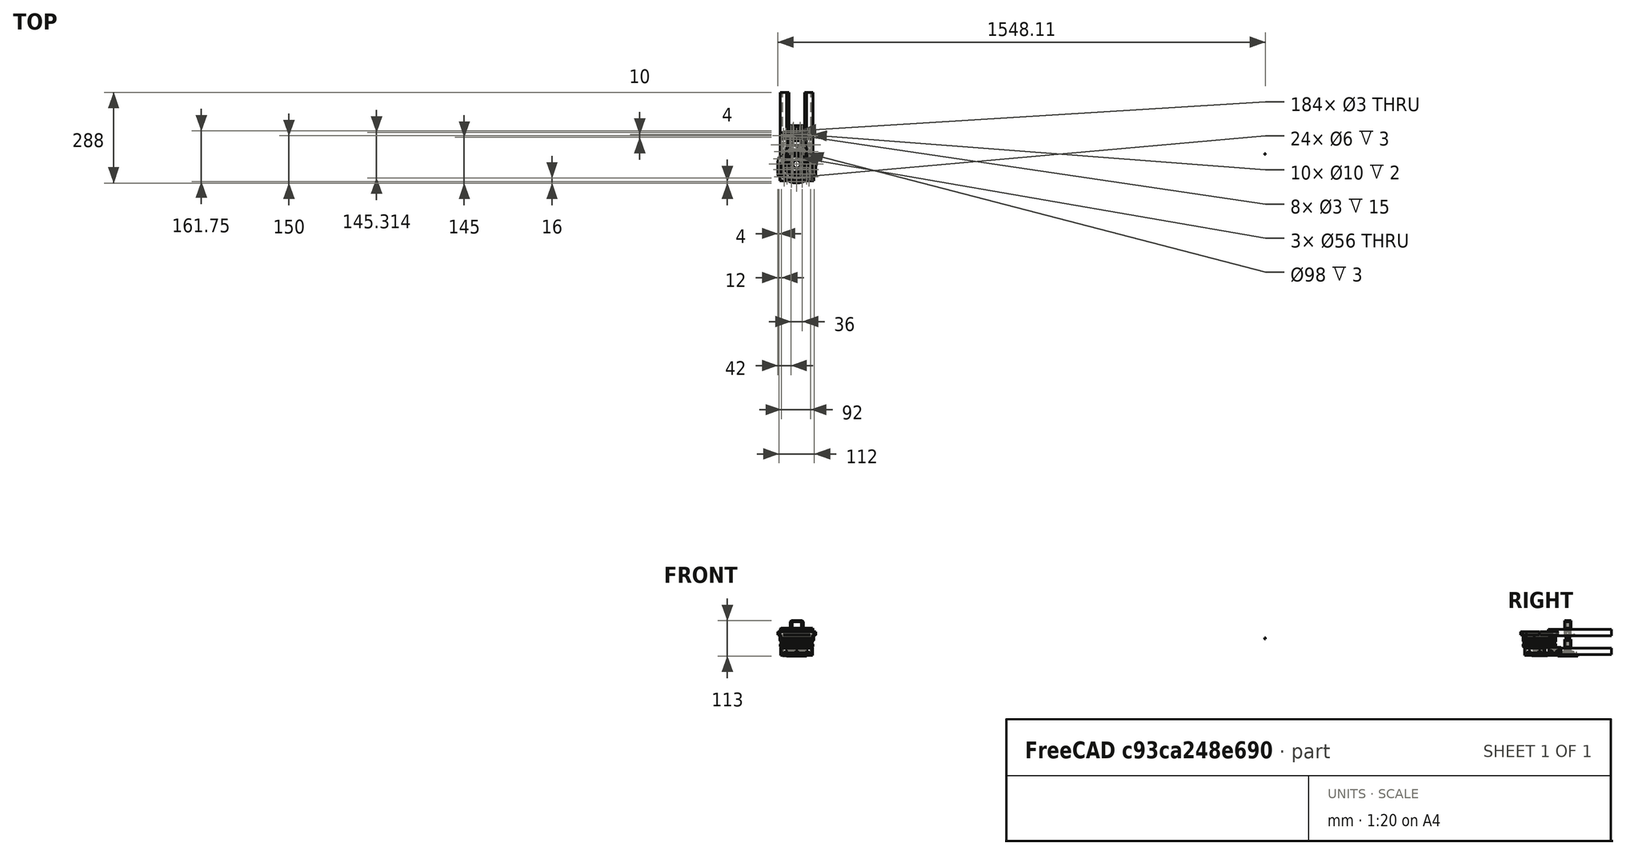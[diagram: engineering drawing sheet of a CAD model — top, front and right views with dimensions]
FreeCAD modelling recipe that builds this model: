
FCSTD DOCUMENT  (FreeCAD 0.19R24276 (Git))
Label: J-midi_encoder_002
License: All rights reserved
LicenseURL: http://en.wikipedia.org/wiki/All_rights_reserved
objects: Part::Cylinder×313, Part::Compound×126, Part::Cut×123, Part::Box×111, Part::Chamfer×32, Part::FeaturePython×23, Part::MultiFuse×6, Mesh::Feature×6, Part::Fillet×5, Part::Mirroring×2
note: 741 computed .brp shape members not serialized (recipe doc carries the construction recipe); baked Part::Feature solids carry a one-line shape summary decoded from their .brp

FEATURE [Part::Cylinder] Cylinder120  label="Válec120"
  Angle = 360
  AttacherType = Attacher::AttachEngine3D
  Height = 10
  Radius = 52
FEATURE [Part::Cylinder] Cylinder121  label="Válec121"
  Angle = 360
  AttacherType = Attacher::AttachEngine3D
  Height = 10
  Radius = 60
FEATURE [Part::FeaturePython] wormgear026  # WARN: FeaturePython — macro-defined, semantics opaque (R4)
  AttacherType = Attacher::AttachEngine3D
  beta = 29.7292
  clearance = 0.25
  diameter = 78.8
  head = 0
  height = 20
  module = 1
  pressure_angle = 20
  reverse_pitch = true
  teeth = 45
  version = 0.0.3
FEATURE [Part::Cut] Cut057
  Base = -> Cylinder121
  Placement = pos=(0,0,10) rot=(0,0,1;0.034907rad)
  Tool = -> wormgear026
FEATURE [Part::FeaturePython] wormgear027  # WARN: FeaturePython — macro-defined, semantics opaque (R4)
  AttacherType = Attacher::AttachEngine3D
  Placement = pos=(0,0,0) rot=(0,0,1;0.009355rad)
  beta = 29.7292
  clearance = 0.25
  diameter = 78.8
  head = 0
  height = 20
  module = 1
  pressure_angle = 20
  reverse_pitch = false
  teeth = 45
  version = 0.0.3
FEATURE [Part::Cut] Cut056
  Base = -> Cylinder120
  Tool = -> wormgear027
FEATURE [Part::Compound] Compound157
  Links = -> [Cut057,Cut056]
FEATURE [Part::Cylinder] Cylinder132  label="Válec132"
  Angle = 360
  AttacherType = Attacher::AttachEngine3D
  Height = 40
  Placement = pos=(59,-17,0) rot=(0,0,1;0rad)
  Radius = 10
FEATURE [Part::Cylinder] Cylinder133  label="Válec133"
  Angle = 360
  AttacherType = Attacher::AttachEngine3D
  Height = 40
  Placement = pos=(-59,-17,0) rot=(0,0,1;0rad)
  Radius = 10
FEATURE [Part::Compound] Compound162
  Links = -> [Cylinder132,Cylinder133]
FEATURE [Part::Cylinder] Cylinder134  label="Válec134"
  Angle = 360
  AttacherType = Attacher::AttachEngine3D
  Height = 10
  Placement = pos=(0,0,20) rot=(0,0,1;0rad)
  Radius = 52
FEATURE [Part::Box] Box045  label="Krychle045"
  AttacherType = Attacher::AttachEngine3D
  Height = 10
  Length = 108
  Placement = pos=(-54,-53,20) rot=(0,0,1;0rad)
  Width = 36
FEATURE [Part::Cut] Cut062
  Base = -> Box045
  Placement = pos=(0,0,-20) rot=(0,0,1;0rad)
  Tool = -> Cylinder134
FEATURE [Part::Cut] Cut063
  Base = -> Cut062
  Tool = -> Compound162
FEATURE [Part::Cylinder] Cylinder135  label="Válec135"
  Angle = 360
  AttacherType = Attacher::AttachEngine3D
  Height = 10
  Placement = pos=(0,0,20) rot=(0,0,1;0rad)
  Radius = 52
FEATURE [Part::Box] Box046  label="Krychle046"
  AttacherType = Attacher::AttachEngine3D
  Height = 10
  Length = 108
  Placement = pos=(-54,-53,20) rot=(0,0,1;0rad)
  Width = 36
FEATURE [Part::Cut] Cut064
  Base = -> Box046
  Placement = pos=(0,0,-10) rot=(0,0,1;0rad)
  Tool = -> Cylinder135
FEATURE [Part::Cylinder] Cylinder136  label="Válec136"
  Angle = 360
  AttacherType = Attacher::AttachEngine3D
  Height = 20
  Placement = pos=(-24,-40,-5) rot=(1,0,0;1.5708rad)
  Radius = 1.5
FEATURE [Part::Cylinder] Cylinder137  label="Válec137"
  Angle = 360
  AttacherType = Attacher::AttachEngine3D
  Height = 20
  Placement = pos=(24,-40,-5) rot=(1,0,0;1.5708rad)
  Radius = 1.5
FEATURE [Part::Box] Box047  label="Krychle047"
  AttacherType = Attacher::AttachEngine3D
  Height = 6
  Length = 6
  Placement = pos=(-27,-47,-8) rot=(0,0,1;0rad)
  Width = 2
FEATURE [Part::Box] Box048  label="Krychle048"
  AttacherType = Attacher::AttachEngine3D
  Height = 6
  Length = 6
  Placement = pos=(21,-47,-8) rot=(0,0,1;0rad)
  Width = 2
FEATURE [Part::FeaturePython] Tube  # WARN: FeaturePython — macro-defined, semantics opaque (R4)
  AttacherType = Attacher::AttachEngine3D
  Height = 8
  InnerRadius = 42
  OuterRadius = 52
  Placement = pos=(0,0,-8) rot=(0,0,1;0rad)
FEATURE [Part::Box] Box049  label="Krychle049"
  AttacherType = Attacher::AttachEngine3D
  Height = 6
  Length = 6
  Placement = pos=(48,-45,4) rot=(0,0,1;0rad)
  Width = 2
FEATURE [Part::Cylinder] Cylinder138  label="Válec138"
  Angle = 360
  AttacherType = Attacher::AttachEngine3D
  Height = 40
  Placement = pos=(59,-17,0) rot=(0,0,1;0rad)
  Radius = 10
FEATURE [Part::Cylinder] Cylinder139  label="Válec139"
  Angle = 360
  AttacherType = Attacher::AttachEngine3D
  Height = 40
  Placement = pos=(-59,-17,0) rot=(0,0,1;0rad)
  Radius = 10
FEATURE [Part::Cylinder] Cylinder140  label="Válec140"
  Angle = 360
  AttacherType = Attacher::AttachEngine3D
  Height = 8
  Placement = pos=(0,0,20) rot=(0,0,1;0rad)
  Radius = 52
FEATURE [Part::Compound] Compound163
  Links = -> [Cylinder138,Cylinder139]
FEATURE [Part::Box] Box050  label="Krychle050"
  AttacherType = Attacher::AttachEngine3D
  Height = 8
  Length = 108
  Placement = pos=(-54,-53,20) rot=(0,0,1;0rad)
  Width = 36
FEATURE [Part::Cut] Cut065
  Base = -> Box050
  Placement = pos=(0,0,-20) rot=(0,0,1;0rad)
  Tool = -> Cylinder140
FEATURE [Part::Cut] Cut066
  Base = -> Cut065
  Placement = pos=(0,0,-8) rot=(0,0,1;0rad)
  Tool = -> Compound163
FEATURE [Part::Cylinder] Cylinder141  label="Válec141"
  Angle = 360
  AttacherType = Attacher::AttachEngine3D
  Height = 20
  Placement = pos=(51,-40,7) rot=(1,0,0;1.5708rad)
  Radius = 1.5
FEATURE [Part::Box] Box051  label="Krychle051"
  AttacherType = Attacher::AttachEngine3D
  Height = 6
  Length = 6
  Placement = pos=(-54,-45,4) rot=(0,0,1;0rad)
  Width = 2
FEATURE [Part::Compound] Compound169
  Links = -> [Box047,Box048,Box049,Box051]
FEATURE [Part::Cylinder] Cylinder142  label="Válec142"
  Angle = 360
  AttacherType = Attacher::AttachEngine3D
  Height = 20
  Placement = pos=(-51,-40,7) rot=(1,0,0;1.5708rad)
  Radius = 1.5
FEATURE [Part::Compound] Compound172
  Links = -> [Cylinder136,Cylinder137,Cylinder141,Cylinder142]
FEATURE [Part::Cylinder] Cylinder143  label="Válec143"
  Angle = 360
  AttacherType = Attacher::AttachEngine3D
  Height = 20
  Placement = pos=(0,-56,2) rot=(0,0,1;0rad)
  Radius = 1.5
FEATURE [Part::Cylinder] Cylinder144  label="Válec144"
  Angle = 360
  AttacherType = Attacher::AttachEngine3D
  Height = 20
  Placement = pos=(39.598,-39.598,2) rot=(0,0,1;0.785398rad)
  Radius = 1.5
FEATURE [Part::Cylinder] Cylinder145  label="Válec145"
  Angle = 360
  AttacherType = Attacher::AttachEngine3D
  Height = 20
  Placement = pos=(56,0,2) rot=(0,0,1;1.5708rad)
  Radius = 1.5
FEATURE [Part::Cylinder] Cylinder146  label="Válec146"
  Angle = 360
  AttacherType = Attacher::AttachEngine3D
  Height = 20
  Placement = pos=(39.598,39.598,2) rot=(0,0,1;2.35619rad)
  Radius = 1.5
FEATURE [Part::Cylinder] Cylinder147  label="Válec147"
  Angle = 360
  AttacherType = Attacher::AttachEngine3D
  Height = 20
  Placement = pos=(-1.2e-14,56,2) rot=(0,0,1;3.14159rad)
  Radius = 1.5
FEATURE [Part::Cylinder] Cylinder148  label="Válec148"
  Angle = 360
  AttacherType = Attacher::AttachEngine3D
  Height = 20
  Placement = pos=(-39.598,39.598,2) rot=(0,0,1;3.92699rad)
  Radius = 1.5
FEATURE [Part::Cylinder] Cylinder149  label="Válec149"
  Angle = 360
  AttacherType = Attacher::AttachEngine3D
  Height = 20
  Placement = pos=(-56,-1.3e-14,2) rot=(0,0,-1;1.5708rad)
  Radius = 1.5
FEATURE [Part::Cylinder] Cylinder150  label="Válec150"
  Angle = 360
  AttacherType = Attacher::AttachEngine3D
  Height = 20
  Placement = pos=(-39.598,-39.598,2) rot=(0,0,-1;0.785398rad)
  Radius = 1.5
FEATURE [Part::Compound] Compound164
  Links = -> [Cylinder143,Cylinder144,Cylinder145,Cylinder146,Cylinder147,Cylinder148,Cylinder149,Cylinder150]
FEATURE [Part::Cut] Cut067
  Base = -> Compound157
  Tool = -> Compound164
FEATURE [Part::Cylinder] Cylinder151  label="Válec151"
  Angle = 360
  AttacherType = Attacher::AttachEngine3D
  Height = 20
  Placement = pos=(-39.598,39.598,2) rot=(0,0,1;3.92699rad)
  Radius = 1.5
FEATURE [Part::Cylinder] Cylinder152  label="Válec152"
  Angle = 360
  AttacherType = Attacher::AttachEngine3D
  Height = 20
  Placement = pos=(-39.598,-39.598,2) rot=(0,0,-1;0.785398rad)
  Radius = 1.5
FEATURE [Part::Cylinder] Cylinder153  label="Válec153"
  Angle = 360
  AttacherType = Attacher::AttachEngine3D
  Height = 20
  Placement = pos=(56,0,2) rot=(0,0,1;1.5708rad)
  Radius = 1.5
FEATURE [Part::Cylinder] Cylinder154  label="Válec154"
  Angle = 360
  AttacherType = Attacher::AttachEngine3D
  Height = 20
  Placement = pos=(-1.2e-14,56,2) rot=(0,0,1;3.14159rad)
  Radius = 1.5
FEATURE [Part::Cylinder] Cylinder155  label="Válec155"
  Angle = 360
  AttacherType = Attacher::AttachEngine3D
  Height = 20
  Placement = pos=(0,-56,2) rot=(0,0,1;0rad)
  Radius = 1.5
FEATURE [Part::Cylinder] Cylinder156  label="Válec156"
  Angle = 360
  AttacherType = Attacher::AttachEngine3D
  Height = 20
  Placement = pos=(39.598,39.598,2) rot=(0,0,1;2.35619rad)
  Radius = 1.5
FEATURE [Part::Cylinder] Cylinder157  label="Válec157"
  Angle = 360
  AttacherType = Attacher::AttachEngine3D
  Height = 20
  Placement = pos=(-56,-1.3e-14,2) rot=(0,0,-1;1.5708rad)
  Radius = 1.5
FEATURE [Part::Cylinder] Cylinder158  label="Válec158"
  Angle = 360
  AttacherType = Attacher::AttachEngine3D
  Height = 20
  Placement = pos=(39.598,-39.598,2) rot=(0,0,1;0.785398rad)
  Radius = 1.5
FEATURE [Part::Compound] Compound165
  Links = -> [Cylinder155,Cylinder158,Cylinder153,Cylinder156,Cylinder154,Cylinder151,Cylinder157,Cylinder152]
FEATURE [Part::Cut] Cut068
  Base = -> Cut064
  Tool = -> Compound165
FEATURE [Part::Cylinder] Cylinder159  label="Válec159"
  Angle = 360
  AttacherType = Attacher::AttachEngine3D
  Height = 20
  Placement = pos=(-39.6,-39.6,-10) rot=(0,0,-1;0.785398rad)
  Radius = 4
FEATURE [Part::Cylinder] Cylinder160  label="Válec160"
  Angle = 360
  AttacherType = Attacher::AttachEngine3D
  Height = 20
  Placement = pos=(39.6,-39.6,-10) rot=(0,0,1;0.785398rad)
  Radius = 4
FEATURE [Part::Compound] Compound166
  Links = -> [Cylinder159,Cylinder160]
FEATURE [Part::Cylinder] Cylinder161  label="Válec161"
  Angle = 360
  AttacherType = Attacher::AttachEngine3D
  Height = 20
  Placement = pos=(39.6,-39.6,-10) rot=(0,0,1;0.785398rad)
  Radius = 4
FEATURE [Part::Cylinder] Cylinder162  label="Válec162"
  Angle = 360
  AttacherType = Attacher::AttachEngine3D
  Height = 20
  Placement = pos=(-39.6,-39.6,-10) rot=(0,0,-1;0.785398rad)
  Radius = 4
FEATURE [Part::Compound] Compound167
  Links = -> [Cylinder162,Cylinder161]
FEATURE [Part::Cut] Cut069
  Base = -> Cut067
  Tool = -> Compound166
FEATURE [Part::Cut] Cut070
  Base = -> Cut066
  Tool = -> Compound167
FEATURE [Part::Cut] Cut072
  Base = -> Cut070
  Tool = -> Compound169
FEATURE [Part::Cylinder] Cylinder163  label="Válec163"
  Angle = 360
  AttacherType = Attacher::AttachEngine3D
  Height = 20
  Placement = pos=(39.6,-39.6,-10) rot=(0,0,1;0.785398rad)
  Radius = 4
FEATURE [Part::Cylinder] Cylinder164  label="Válec164"
  Angle = 360
  AttacherType = Attacher::AttachEngine3D
  Height = 20
  Placement = pos=(-39.6,-39.6,-10) rot=(0,0,-1;0.785398rad)
  Radius = 4
FEATURE [Part::Compound] Compound168
  Links = -> [Cylinder164,Cylinder163]
FEATURE [Part::Cut] Cut071
  Base = -> Cut063
  Tool = -> Compound168
FEATURE [Part::Box] Box052  label="Krychle052"
  AttacherType = Attacher::AttachEngine3D
  Height = 6
  Length = 6
  Placement = pos=(48,-45,4) rot=(0,0,1;0rad)
  Width = 2
FEATURE [Part::Box] Box053  label="Krychle053"
  AttacherType = Attacher::AttachEngine3D
  Height = 6
  Length = 6
  Placement = pos=(17,-47,-8) rot=(0,0,1;0rad)
  Width = 2
FEATURE [Part::Box] Box054  label="Krychle054"
  AttacherType = Attacher::AttachEngine3D
  Height = 6
  Length = 6
  Placement = pos=(-23,-47,-8) rot=(0,0,1;0rad)
  Width = 2
FEATURE [Part::Box] Box055  label="Krychle055"
  AttacherType = Attacher::AttachEngine3D
  Height = 6
  Length = 6
  Placement = pos=(-54,-45,4) rot=(0,0,1;0rad)
  Width = 2
FEATURE [Part::Compound] Compound170
  Links = -> [Box054,Box053,Box052,Box055]
FEATURE [Part::Cut] Cut073
  Base = -> Cut071
  Tool = -> Compound170
FEATURE [Part::Box] Box056  label="Krychle056"
  AttacherType = Attacher::AttachEngine3D
  Height = 6
  Length = 6
  Placement = pos=(48,-45,4) rot=(0,0,1;0rad)
  Width = 2
FEATURE [Part::Box] Box057  label="Krychle057"
  AttacherType = Attacher::AttachEngine3D
  Height = 6
  Length = 6
  Placement = pos=(21,-47,-8) rot=(0,0,1;0rad)
  Width = 2
FEATURE [Part::Box] Box058  label="Krychle058"
  AttacherType = Attacher::AttachEngine3D
  Height = 6
  Length = 6
  Placement = pos=(-27,-47,-8) rot=(0,0,1;0rad)
  Width = 2
FEATURE [Part::Box] Box059  label="Krychle059"
  AttacherType = Attacher::AttachEngine3D
  Height = 6
  Length = 6
  Placement = pos=(-54,-45,4) rot=(0,0,1;0rad)
  Width = 2
FEATURE [Part::Compound] Compound171
  Links = -> [Box058,Box057,Box056,Box059]
FEATURE [Part::Cylinder] Cylinder165  label="Válec165"
  Angle = 360
  AttacherType = Attacher::AttachEngine3D
  Height = 20
  Placement = pos=(-24,-40,-5) rot=(1,0,0;1.5708rad)
  Radius = 1.5
FEATURE [Part::Cylinder] Cylinder166  label="Válec166"
  Angle = 360
  AttacherType = Attacher::AttachEngine3D
  Height = 20
  Placement = pos=(24,-40,-5) rot=(1,0,0;1.5708rad)
  Radius = 1.5
FEATURE [Part::Cut] Cut074
  Base = -> Tube
  Tool = -> Compound171
FEATURE [Part::Cut] Cut075
  Base = -> Cut074
  Tool = -> Compound172
FEATURE [Part::Cylinder] Cylinder167  label="Válec167"
  Angle = 360
  AttacherType = Attacher::AttachEngine3D
  Height = 20
  Placement = pos=(51,-40,7) rot=(1,0,0;1.5708rad)
  Radius = 1.5
FEATURE [Part::Cylinder] Cylinder168  label="Válec168"
  Angle = 360
  AttacherType = Attacher::AttachEngine3D
  Height = 20
  Placement = pos=(-51,-40,7) rot=(1,0,0;1.5708rad)
  Radius = 1.5
FEATURE [Part::Compound] Compound173
  Links = -> [Cylinder165,Cylinder166,Cylinder167,Cylinder168]
FEATURE [Part::Cut] Cut076
  Base = -> Cut072
  Tool = -> Compound173
FEATURE [Part::Cylinder] Cylinder169  label="Válec169"
  Angle = 360
  AttacherType = Attacher::AttachEngine3D
  Height = 20
  Placement = pos=(-20,-40,-5) rot=(1,0,0;1.5708rad)
  Radius = 1.5
FEATURE [Part::Cylinder] Cylinder170  label="Válec170"
  Angle = 360
  AttacherType = Attacher::AttachEngine3D
  Height = 20
  Placement = pos=(20,-40,-5) rot=(1,0,0;1.5708rad)
  Radius = 1.5
FEATURE [Part::Cylinder] Cylinder171  label="Válec171"
  Angle = 360
  AttacherType = Attacher::AttachEngine3D
  Height = 20
  Placement = pos=(51,-40,7) rot=(1,0,0;1.5708rad)
  Radius = 1.5
FEATURE [Part::Cylinder] Cylinder172  label="Válec172"
  Angle = 360
  AttacherType = Attacher::AttachEngine3D
  Height = 20
  Placement = pos=(-51,-40,7) rot=(1,0,0;1.5708rad)
  Radius = 1.5
FEATURE [Part::Compound] Compound174
  Links = -> [Cylinder169,Cylinder170,Cylinder171,Cylinder172]
FEATURE [Part::Cut] Cut077
  Base = -> Cut073
  Tool = -> Compound174
FEATURE [Part::Box] Box060  label="Krychle060"
  AttacherType = Attacher::AttachEngine3D
  Height = 2
  Length = 6
  Placement = pos=(-3,41,-4) rot=(0,0,1;0rad)
  Width = 8
FEATURE [Part::Cylinder] Cylinder173  label="Válec173"
  Angle = 360
  AttacherType = Attacher::AttachEngine3D
  Height = 20
  Placement = pos=(0,45,-18) rot=(0,0,1;0rad)
  Radius = 1.5
FEATURE [Part::Box] Box061  label="Krychle061"
  AttacherType = Attacher::AttachEngine3D
  Height = 2
  Length = 6
  Placement = pos=(-31.1127,26.8701,-4) rot=(0,0,1;0.785398rad)
  Width = 8
FEATURE [Part::Box] Box062  label="Krychle062"
  AttacherType = Attacher::AttachEngine3D
  Height = 2
  Length = 6
  Placement = pos=(-41,-3,-4) rot=(0,0,1;1.5708rad)
  Width = 8
FEATURE [Part::Box] Box063  label="Krychle063"
  AttacherType = Attacher::AttachEngine3D
  Height = 2
  Length = 6
  Placement = pos=(-26.8701,-31.1127,-4) rot=(0,0,1;2.35619rad)
  Width = 8
FEATURE [Part::Box] Box064  label="Krychle064"
  AttacherType = Attacher::AttachEngine3D
  Height = 2
  Length = 6
  Placement = pos=(3,-41,-4) rot=(0,0,1;3.14159rad)
  Width = 8
FEATURE [Part::Box] Box065  label="Krychle065"
  AttacherType = Attacher::AttachEngine3D
  Height = 2
  Length = 6
  Placement = pos=(31.1127,-26.8701,-4) rot=(0,0,1;3.92699rad)
  Width = 8
FEATURE [Part::Box] Box066  label="Krychle066"
  AttacherType = Attacher::AttachEngine3D
  Height = 2
  Length = 6
  Placement = pos=(41,3,-4) rot=(0,0,-1;1.5708rad)
  Width = 8
FEATURE [Part::Box] Box067  label="Krychle067"
  AttacherType = Attacher::AttachEngine3D
  Height = 2
  Length = 6
  Placement = pos=(26.8701,31.1127,-4) rot=(0,0,-1;0.785398rad)
  Width = 8
FEATURE [Part::Cylinder] Cylinder174  label="Válec174"
  Angle = 360
  AttacherType = Attacher::AttachEngine3D
  Height = 20
  Placement = pos=(-31.8198,31.8198,-18) rot=(0,0,1;0.785398rad)
  Radius = 1.5
FEATURE [Part::Cylinder] Cylinder175  label="Válec175"
  Angle = 360
  AttacherType = Attacher::AttachEngine3D
  Height = 20
  Placement = pos=(-45,-6e-15,-18) rot=(0,0,1;1.5708rad)
  Radius = 1.5
FEATURE [Part::Cylinder] Cylinder176  label="Válec176"
  Angle = 360
  AttacherType = Attacher::AttachEngine3D
  Height = 20
  Placement = pos=(-31.8198,-31.8198,-18) rot=(0,0,1;2.35619rad)
  Radius = 1.5
FEATURE [Part::Cylinder] Cylinder177  label="Válec177"
  Angle = 360
  AttacherType = Attacher::AttachEngine3D
  Height = 20
  Placement = pos=(1.4e-14,-45,-18) rot=(0,0,1;3.14159rad)
  Radius = 1.5
FEATURE [Part::Cylinder] Cylinder178  label="Válec178"
  Angle = 360
  AttacherType = Attacher::AttachEngine3D
  Height = 20
  Placement = pos=(31.8198,-31.8198,-18) rot=(0,0,1;3.92699rad)
  Radius = 1.5
FEATURE [Part::Compound] Compound175
  Links = -> [Box060,Box061,Box062,Box063,Box064,Box065,Box066,Box067]
  Placement = pos=(0,0,0) rot=(0,0,1;0.392699rad)
FEATURE [Part::Cut] Cut078
  Base = -> Cut075
  Tool = -> Compound175
FEATURE [Part::Cylinder] Cylinder179  label="Válec179"
  Angle = 360
  AttacherType = Attacher::AttachEngine3D
  Height = 20
  Placement = pos=(45,1.9e-14,-18) rot=(0,0,-1;1.5708rad)
  Radius = 1.5
FEATURE [Part::Cylinder] Cylinder180  label="Válec180"
  Angle = 360
  AttacherType = Attacher::AttachEngine3D
  Height = 20
  Placement = pos=(31.8198,31.8198,-18) rot=(0,0,-1;0.785398rad)
  Radius = 1.5
FEATURE [Part::Compound] Compound176
  Links = -> [Cylinder173,Cylinder174,Cylinder175,Cylinder176,Cylinder177,Cylinder178,Cylinder179,Cylinder180]
  Placement = pos=(0,0,0) rot=(0,0,1;0.392699rad)
FEATURE [Part::Cut] Cut079
  Base = -> Cut078
  Tool = -> Compound176
FEATURE [Part::Compound] Compound177  label="joint_max_monoblok1"
  Links = -> [Cut077,Cut079,Cut076,Cut069,Cut068]
FEATURE [Part::Fillet] Fillet
  Base = -> Compound177
  Edges = 2 edges r=9: [Edge42,Edge278]
FEATURE [Part::Fillet] Fillet001  label="J-max_monoblok2"
  Base = -> Fillet
  Edges = 2 edges r=8: [Edge30,Edge90]
FEATURE [Part::Box] Box108  label="Krychle108"
  AttacherType = Attacher::AttachEngine3D
  Height = 10
  Length = 10
  Placement = pos=(50,-43,10) rot=(0,0,1;0rad)
  Width = 43
FEATURE [Part::Cylinder] Cylinder300  label="Válec300"
  Angle = 360
  AttacherType = Attacher::AttachEngine3D
  Height = 10
  Placement = pos=(60,-43,10) rot=(0,0,1;0rad)
  Radius = 6
FEATURE [Part::Box] Box109  label="Krychle109"
  AttacherType = Attacher::AttachEngine3D
  Height = 10
  Length = 10
  Placement = pos=(-60,-43,10) rot=(0,0,1;0rad)
  Width = 43
FEATURE [Part::Cylinder] Cylinder301  label="Válec301"
  Angle = 360
  AttacherType = Attacher::AttachEngine3D
  Height = 10
  Placement = pos=(-60,-43,10) rot=(0,0,1;0rad)
  Radius = 6
FEATURE [Part::Cylinder] Cylinder302  label="Válec302"
  Angle = 360
  AttacherType = Attacher::AttachEngine3D
  Height = 20
  Placement = pos=(39.598,-39.598,2) rot=(0,0,1;0.785398rad)
  Radius = 1.5
FEATURE [Part::Cylinder] Cylinder303  label="Válec303"
  Angle = 360
  AttacherType = Attacher::AttachEngine3D
  Height = 20
  Placement = pos=(39.598,39.598,2) rot=(0,0,1;2.35619rad)
  Radius = 1.5
FEATURE [Part::Compound] Compound239
  Links = -> [Box109,Box108]
FEATURE [Part::Compound] Compound241
  Links = -> [Cylinder300,Cylinder301]
FEATURE [Part::Cylinder] Cylinder304  label="Válec304"
  Angle = 360
  AttacherType = Attacher::AttachEngine3D
  Height = 20
  Placement = pos=(-39.598,39.598,2) rot=(0,0,1;3.92699rad)
  Radius = 1.5
FEATURE [Part::Cylinder] Cylinder305  label="Válec305"
  Angle = 360
  AttacherType = Attacher::AttachEngine3D
  Height = 20
  Placement = pos=(-39.598,-39.598,2) rot=(0,0,-1;0.785398rad)
  Radius = 1.5
FEATURE [Part::Cylinder] Cylinder306  label="Válec306"
  Angle = 360
  AttacherType = Attacher::AttachEngine3D
  Height = 20
  Placement = pos=(56,0,2) rot=(0,0,1;1.5708rad)
  Radius = 1.5
FEATURE [Part::Cylinder] Cylinder307  label="Válec307"
  Angle = 360
  AttacherType = Attacher::AttachEngine3D
  Height = 20
  Placement = pos=(-1.2e-14,56,2) rot=(0,0,1;3.14159rad)
  Radius = 1.5
FEATURE [Part::Cylinder] Cylinder308  label="Válec308"
  Angle = 360
  AttacherType = Attacher::AttachEngine3D
  Height = 20
  Placement = pos=(-56,-1.3e-14,2) rot=(0,0,-1;1.5708rad)
  Radius = 1.5
FEATURE [Part::Cylinder] Cylinder309  label="Válec309"
  Angle = 360
  AttacherType = Attacher::AttachEngine3D
  Height = 20
  Placement = pos=(0,-56,2) rot=(0,0,1;0rad)
  Radius = 1.5
FEATURE [Part::Compound] Compound240
  Links = -> [Cylinder309,Cylinder302,Cylinder306,Cylinder303,Cylinder307,Cylinder304,Cylinder308,Cylinder305]
FEATURE [Part::Cut] Cut129
  Base = -> Compound239
  Tool = -> Compound240
FEATURE [Part::Cut] Cut130
  Base = -> Cut129
  Tool = -> Compound241
FEATURE [Part::Fillet] Fillet002
  Base = -> Cut130
  Edges = 2 edges r=4: [Edge4,Edge43]
FEATURE [Part::Compound] Compound242  label="J-max_monoblok"
  Links = -> [Fillet002,Fillet001]
FEATURE [Part::Cylinder] Cylinder623  label="Válec623"
  Angle = 360
  AttacherType = Attacher::AttachEngine3D
  Height = 20
  Placement = pos=(-31.8198,31.8198,-18) rot=(0,0,1;0.785398rad)
  Radius = 1.5
FEATURE [Part::Cylinder] Cylinder625  label="Válec625"
  Angle = 360
  AttacherType = Attacher::AttachEngine3D
  Height = 16
  Placement = pos=(2e-15,16,2) rot=(0,0,-1;1.1781rad)
  Radius = 1.5
FEATURE [Part::Cylinder] Cylinder626  label="Válec626"
  Angle = 360
  AttacherType = Attacher::AttachEngine3D
  Height = 16
  Placement = pos=(-16,7e-15,2) rot=(0,0,1;0.392699rad)
  Radius = 1.5
FEATURE [Part::Cylinder] Cylinder627  label="Válec627"
  Angle = 360
  AttacherType = Attacher::AttachEngine3D
  Height = 16
  Placement = pos=(-1.2e-14,-16,2) rot=(0,0,1;1.96349rad)
  Radius = 1.5
FEATURE [Part::Cylinder] Cylinder628  label="Válec628"
  Angle = 360
  AttacherType = Attacher::AttachEngine3D
  Height = 20
  Placement = pos=(0,45,-18) rot=(0,0,1;0rad)
  Radius = 1.5
FEATURE [Part::Cylinder] Cylinder629  label="Válec629"
  Angle = 360
  AttacherType = Attacher::AttachEngine3D
  Height = 20
  Placement = pos=(-31.8198,-31.8198,-18) rot=(0,0,1;2.35619rad)
  Radius = 1.5
FEATURE [Part::Cylinder] Cylinder630  label="Válec630"
  Angle = 360
  AttacherType = Attacher::AttachEngine3D
  Height = 16
  Placement = pos=(16,0,2) rot=(0,0,1;3.53429rad)
  Radius = 1.5
FEATURE [Part::Compound] Compound653
  Links = -> [Cylinder630,Cylinder625,Cylinder626,Cylinder627]
  Placement = pos=(0,0,-111) rot=(0,0,1;0rad)
FEATURE [Part::Cylinder] Cylinder631  label="Válec631"
  Angle = 360
  AttacherType = Attacher::AttachEngine3D
  Height = 20
  Placement = pos=(45,1.9e-14,-18) rot=(0,0,-1;1.5708rad)
  Radius = 1.5
FEATURE [Part::Cylinder] Cylinder632  label="Válec632"
  Angle = 360
  AttacherType = Attacher::AttachEngine3D
  Height = 20
  Placement = pos=(-45,-6e-15,-18) rot=(0,0,1;1.5708rad)
  Radius = 1.5
FEATURE [Part::Cylinder] Cylinder633  label="Válec633"
  Angle = 360
  AttacherType = Attacher::AttachEngine3D
  Height = 20
  Placement = pos=(31.8198,31.8198,-18) rot=(0,0,-1;0.785398rad)
  Radius = 1.5
FEATURE [Part::Cylinder] Cylinder638  label="Válec638"
  Angle = 360
  AttacherType = Attacher::AttachEngine3D
  Height = 20
  Placement = pos=(31.8198,-31.8198,-18) rot=(0,0,1;3.92699rad)
  Radius = 1.5
FEATURE [Part::Cylinder] Cylinder639  label="Válec639"
  Angle = 360
  AttacherType = Attacher::AttachEngine3D
  Height = 20
  Placement = pos=(1.4e-14,-45,-18) rot=(0,0,1;3.14159rad)
  Radius = 1.5
FEATURE [Part::Compound] Compound654
  Links = -> [Cylinder628,Cylinder623,Cylinder632,Cylinder629,Cylinder639,Cylinder638,Cylinder631,Cylinder633]
  Placement = pos=(0,0,-87) rot=(0,0,1;0.392699rad)
FEATURE [Part::FeaturePython] Tube038  # WARN: FeaturePython — macro-defined, semantics opaque (R4)
  AttacherType = Attacher::AttachEngine3D
  Height = 2
  InnerRadius = 12
  OuterRadius = 52
  Placement = pos=(0,0,-100) rot=(0,0,1;0rad)
FEATURE [Part::FeaturePython] Tube040  # WARN: FeaturePython — macro-defined, semantics opaque (R4)
  AttacherType = Attacher::AttachEngine3D
  Height = 3
  InnerRadius = 42
  OuterRadius = 52
  Placement = pos=(0,0,-11) rot=(0,0,1;0rad)
FEATURE [Part::Cut] Cut285
  Base = -> Tube038
  Tool = -> Compound653
FEATURE [Part::Cut] Cut287
  Base = -> Cut285
  Tool = -> Compound654
FEATURE [Part::Cylinder] Cylinder652  label="Válec652"
  Angle = 360
  AttacherType = Attacher::AttachEngine3D
  Height = 20
  Placement = pos=(-31.8198,-31.8198,-18) rot=(0,0,1;2.35619rad)
  Radius = 1.5
FEATURE [Part::Cylinder] Cylinder653  label="Válec653"
  Angle = 360
  AttacherType = Attacher::AttachEngine3D
  Height = 20
  Placement = pos=(0,45,-18) rot=(0,0,1;0rad)
  Radius = 1.5
FEATURE [Part::Cylinder] Cylinder654  label="Válec654"
  Angle = 360
  AttacherType = Attacher::AttachEngine3D
  Height = 20
  Placement = pos=(45,1.9e-14,-18) rot=(0,0,-1;1.5708rad)
  Radius = 1.5
FEATURE [Part::Cylinder] Cylinder655  label="Válec655"
  Angle = 360
  AttacherType = Attacher::AttachEngine3D
  Height = 20
  Placement = pos=(1.4e-14,-45,-18) rot=(0,0,1;3.14159rad)
  Radius = 1.5
FEATURE [Part::Cylinder] Cylinder656  label="Válec656"
  Angle = 360
  AttacherType = Attacher::AttachEngine3D
  Height = 20
  Placement = pos=(31.8198,31.8198,-18) rot=(0,0,-1;0.785398rad)
  Radius = 1.5
FEATURE [Part::Cylinder] Cylinder657  label="Válec657"
  Angle = 360
  AttacherType = Attacher::AttachEngine3D
  Height = 20
  Placement = pos=(31.8198,-31.8198,-18) rot=(0,0,1;3.92699rad)
  Radius = 1.5
FEATURE [Part::Cylinder] Cylinder658  label="Válec658"
  Angle = 360
  AttacherType = Attacher::AttachEngine3D
  Height = 20
  Placement = pos=(-31.8198,31.8198,-18) rot=(0,0,1;0.785398rad)
  Radius = 1.5
FEATURE [Part::Cylinder] Cylinder659  label="Válec659"
  Angle = 360
  AttacherType = Attacher::AttachEngine3D
  Height = 20
  Placement = pos=(-45,-6e-15,-18) rot=(0,0,1;1.5708rad)
  Radius = 1.5
FEATURE [Part::Compound] Compound660
  Links = -> [Cylinder653,Cylinder658,Cylinder659,Cylinder652,Cylinder655,Cylinder657,Cylinder654,Cylinder656]
  Placement = pos=(0,0,0) rot=(0,0,1;0.392699rad)
FEATURE [Part::Cut] Cut290  label="J-max_motor-high-washer_A1"
  Base = -> Tube040
  Placement = pos=(0,0,-4) rot=(0,0,1;0rad)
  Tool = -> Compound660
FEATURE [Part::Chamfer] Chamfer018  label="J-max_motor-high-washer_A"
  Base = -> Cut290
  Edges = 1 edges r=1: [Edge3]
  Placement = pos=(0,0,4) rot=(0,0,1;0rad)
FEATURE [Part::Cylinder] Cylinder660  label="Válec660"
  Angle = 360
  AttacherType = Attacher::AttachEngine3D
  Height = 20
  Placement = pos=(0,45,-18) rot=(0,0,1;0rad)
  Radius = 1.5
FEATURE [Part::Cylinder] Cylinder661  label="Válec661"
  Angle = 360
  AttacherType = Attacher::AttachEngine3D
  Height = 20
  Placement = pos=(-31.8198,-31.8198,-18) rot=(0,0,1;2.35619rad)
  Radius = 1.5
FEATURE [Part::Cylinder] Cylinder662  label="Válec662"
  Angle = 360
  AttacherType = Attacher::AttachEngine3D
  Height = 20
  Placement = pos=(-31.8198,31.8198,-18) rot=(0,0,1;0.785398rad)
  Radius = 1.5
FEATURE [Part::Cylinder] Cylinder663  label="Válec663"
  Angle = 360
  AttacherType = Attacher::AttachEngine3D
  Height = 20
  Placement = pos=(1.4e-14,-45,-18) rot=(0,0,1;3.14159rad)
  Radius = 1.5
FEATURE [Part::Cylinder] Cylinder664  label="Válec664"
  Angle = 360
  AttacherType = Attacher::AttachEngine3D
  Height = 20
  Placement = pos=(-45,-6e-15,-18) rot=(0,0,1;1.5708rad)
  Radius = 1.5
FEATURE [Part::Cylinder] Cylinder665  label="Válec665"
  Angle = 360
  AttacherType = Attacher::AttachEngine3D
  Height = 20
  Placement = pos=(45,1.9e-14,-18) rot=(0,0,-1;1.5708rad)
  Radius = 1.5
FEATURE [Part::Cylinder] Cylinder666  label="Válec666"
  Angle = 360
  AttacherType = Attacher::AttachEngine3D
  Height = 20
  Placement = pos=(31.8198,31.8198,-18) rot=(0,0,-1;0.785398rad)
  Radius = 1.5
FEATURE [Part::Cylinder] Cylinder667  label="Válec667"
  Angle = 360
  AttacherType = Attacher::AttachEngine3D
  Height = 20
  Placement = pos=(31.8198,-31.8198,-18) rot=(0,0,1;3.92699rad)
  Radius = 1.5
FEATURE [Part::Compound] Compound661
  Links = -> [Cylinder660,Cylinder662,Cylinder664,Cylinder661,Cylinder663,Cylinder667,Cylinder665,Cylinder666]
  Placement = pos=(0,0,-8) rot=(0,0,1;0.392699rad)
FEATURE [Part::FeaturePython] Tube041  # WARN: FeaturePython — macro-defined, semantics opaque (R4)
  AttacherType = Attacher::AttachEngine3D
  Height = 10
  InnerRadius = 42
  OuterRadius = 49
  Placement = pos=(0,0,-22) rot=(0,0,1;0rad)
FEATURE [Part::Cut] Cut291
  Base = -> Tube041
  Placement = pos=(0,0,-10) rot=(0,0,1;0rad)
  Tool = -> Compound661
FEATURE [Part::FeaturePython] Tube042  # WARN: FeaturePython — macro-defined, semantics opaque (R4)
  AttacherType = Attacher::AttachEngine3D
  Height = 3
  InnerRadius = 49
  OuterRadius = 52
  Placement = pos=(0,0,-22) rot=(0,0,1;0rad)
FEATURE [Part::Chamfer] Chamfer017
  Base = -> Tube042
  Edges = 1 edges r=1: [Edge1]
  Placement = pos=(0,0,-10) rot=(0,0,1;0rad)
FEATURE [Part::Compound] Compound662  label="J-max_motor-high-washer_B"
  Links = -> [Cut291,Chamfer017]
  Placement = pos=(0,0,11) rot=(0,0,1;0rad)
FEATURE [Part::FeaturePython] Tube060  # WARN: FeaturePython — macro-defined, semantics opaque (R4)
  AttacherType = Attacher::AttachEngine3D
  Height = 9
  InnerRadius = 31
  OuterRadius = 36
  Placement = pos=(0,0,-99) rot=(0,0,1;0rad)
FEATURE [Part::Chamfer] Chamfer019
  Base = -> Tube060
  Edges = 1 edges r=1: [Edge4]
FEATURE [Part::FeaturePython] Tube061  # WARN: FeaturePython — macro-defined, semantics opaque (R4)
  AttacherType = Attacher::AttachEngine3D
  Height = 1
  InnerRadius = 26
  OuterRadius = 36
  Placement = pos=(0,0,-98) rot=(0,0,1;0rad)
FEATURE [Part::Compound] Compound663  label="J-max_undermotor-undercover"
  Links = -> [Chamfer019,Tube061,Cut287]
  Placement = pos=(0,0,77) rot=(0,0,1;0rad)
FEATURE [Part::Box] Box104  label="Krychle104"
  AttacherType = Attacher::AttachEngine3D
  Height = 2
  Length = 10
  Placement = pos=(11,-3,6) rot=(0,0,1;0rad)
  Width = 6
FEATURE [Part::Box] Box105  label="Krychle105"
  AttacherType = Attacher::AttachEngine3D
  Height = 2
  Length = 10
  Placement = pos=(-11,3,6) rot=(0,0,1;3.14159rad)
  Width = 6
FEATURE [Part::Box] Box106  label="Krychle106"
  AttacherType = Attacher::AttachEngine3D
  Height = 2
  Length = 10
  Placement = pos=(3,11,6) rot=(0,0,1;1.5708rad)
  Width = 6
FEATURE [Part::Box] Box107  label="Krychle107"
  AttacherType = Attacher::AttachEngine3D
  Height = 2
  Length = 10
  Placement = pos=(-3,-11,6) rot=(0,0,-1;1.5708rad)
  Width = 6
FEATURE [Part::Cylinder] Cylinder272  label="Válec272"
  Angle = 360
  AttacherType = Attacher::AttachEngine3D
  Height = 16
  Placement = pos=(16,0,2) rot=(0,0,1;3.53429rad)
  Radius = 1.5
FEATURE [Part::Compound] Compound232
  Links = -> [Box104,Box106,Box105,Box107]
  Placement = pos=(0,0,-111) rot=(0,0,1;0rad)
FEATURE [Part::FeaturePython] Tube029  # WARN: FeaturePython — macro-defined, semantics opaque (R4)
  AttacherType = Attacher::AttachEngine3D
  Height = 5
  InnerRadius = 12
  OuterRadius = 52
  Placement = pos=(0,0,-100) rot=(0,0,1;0rad)
FEATURE [Part::FeaturePython] Tube030  # WARN: FeaturePython — macro-defined, semantics opaque (R4)
  AttacherType = Attacher::AttachEngine3D
  Height = 4
  InnerRadius = 12
  OuterRadius = 24.8
  Placement = pos=(0,0,-103) rot=(0,0,1;0rad)
FEATURE [Part::FeaturePython] Tube031  # WARN: FeaturePython — macro-defined, semantics opaque (R4)
  AttacherType = Attacher::AttachEngine3D
  Height = 11
  InnerRadius = 12
  OuterRadius = 20
  Placement = pos=(0,0,-111) rot=(0,0,1;0rad)
FEATURE [Part::Cylinder] Cylinder273  label="Válec273"
  Angle = 360
  AttacherType = Attacher::AttachEngine3D
  Height = 16
  Placement = pos=(-16,7e-15,2) rot=(0,0,1;0.392699rad)
  Radius = 1.5
FEATURE [Part::Cylinder] Cylinder274  label="Válec274"
  Angle = 360
  AttacherType = Attacher::AttachEngine3D
  Height = 16
  Placement = pos=(-1.2e-14,-16,2) rot=(0,0,1;1.96349rad)
  Radius = 1.5
FEATURE [Part::Cylinder] Cylinder275  label="Válec275"
  Angle = 360
  AttacherType = Attacher::AttachEngine3D
  Height = 16
  Placement = pos=(2e-15,16,2) rot=(0,0,-1;1.1781rad)
  Radius = 1.5
FEATURE [Part::Compound] Compound233
  Links = -> [Cylinder272,Cylinder275,Cylinder273,Cylinder274]
  Placement = pos=(0,0,-117) rot=(0,0,1;0rad)
FEATURE [Part::Cut] Cut124
  Base = -> Tube030
  Placement = pos=(0,0,-1) rot=(0,0,1;0rad)
  Tool = -> Compound233
FEATURE [Part::Cylinder] Cylinder276  label="Válec276"
  Angle = 360
  AttacherType = Attacher::AttachEngine3D
  Height = 16
  Placement = pos=(16,0,2) rot=(0,0,1;3.53429rad)
  Radius = 1.5
FEATURE [Part::Cylinder] Cylinder277  label="Válec277"
  Angle = 360
  AttacherType = Attacher::AttachEngine3D
  Height = 16
  Placement = pos=(-16,7e-15,2) rot=(0,0,1;0.392699rad)
  Radius = 1.5
FEATURE [Part::Cylinder] Cylinder278  label="Válec278"
  Angle = 360
  AttacherType = Attacher::AttachEngine3D
  Height = 16
  Placement = pos=(-1.2e-14,-16,2) rot=(0,0,1;1.96349rad)
  Radius = 1.5
FEATURE [Part::Cylinder] Cylinder279  label="Válec279"
  Angle = 360
  AttacherType = Attacher::AttachEngine3D
  Height = 16
  Placement = pos=(2e-15,16,2) rot=(0,0,-1;1.1781rad)
  Radius = 1.5
FEATURE [Part::Compound] Compound234
  Links = -> [Cylinder276,Cylinder279,Cylinder277,Cylinder278]
  Placement = pos=(0,0,-117) rot=(0,0,1;0rad)
FEATURE [Part::Cut] Cut123
  Base = -> Tube031
  Tool = -> Compound234
FEATURE [Part::Cut] Cut126
  Base = -> Cut123
  Tool = -> Compound232
FEATURE [Part::Cylinder] Cylinder280  label="Válec280"
  Angle = 360
  AttacherType = Attacher::AttachEngine3D
  Height = 16
  Placement = pos=(2e-15,16,2) rot=(0,0,-1;1.1781rad)
  Radius = 1.5
FEATURE [Part::Cylinder] Cylinder281  label="Válec281"
  Angle = 360
  AttacherType = Attacher::AttachEngine3D
  Height = 16
  Placement = pos=(16,0,2) rot=(0,0,1;3.53429rad)
  Radius = 1.5
FEATURE [Part::Cylinder] Cylinder282  label="Válec282"
  Angle = 360
  AttacherType = Attacher::AttachEngine3D
  Height = 16
  Placement = pos=(-16,7e-15,2) rot=(0,0,1;0.392699rad)
  Radius = 1.5
FEATURE [Part::Cylinder] Cylinder283  label="Válec283"
  Angle = 360
  AttacherType = Attacher::AttachEngine3D
  Height = 16
  Placement = pos=(-1.2e-14,-16,2) rot=(0,0,1;1.96349rad)
  Radius = 1.5
FEATURE [Part::Cylinder] Cylinder284  label="Válec284"
  Angle = 360
  AttacherType = Attacher::AttachEngine3D
  Height = 20
  Placement = pos=(-45,-6e-15,-18) rot=(0,0,1;1.5708rad)
  Radius = 1.5
FEATURE [Part::Cylinder] Cylinder285  label="Válec285"
  Angle = 360
  AttacherType = Attacher::AttachEngine3D
  Height = 20
  Placement = pos=(-31.8198,-31.8198,-18) rot=(0,0,1;2.35619rad)
  Radius = 1.5
FEATURE [Part::Cylinder] Cylinder286  label="Válec286"
  Angle = 360
  AttacherType = Attacher::AttachEngine3D
  Height = 20
  Placement = pos=(0,45,-18) rot=(0,0,1;0rad)
  Radius = 1.5
FEATURE [Part::Cylinder] Cylinder287  label="Válec287"
  Angle = 360
  AttacherType = Attacher::AttachEngine3D
  Height = 20
  Placement = pos=(45,1.9e-14,-18) rot=(0,0,-1;1.5708rad)
  Radius = 1.5
FEATURE [Part::Cylinder] Cylinder288  label="Válec288"
  Angle = 360
  AttacherType = Attacher::AttachEngine3D
  Height = 20
  Placement = pos=(-31.8198,31.8198,-18) rot=(0,0,1;0.785398rad)
  Radius = 1.5
FEATURE [Part::Cylinder] Cylinder289  label="Válec289"
  Angle = 360
  AttacherType = Attacher::AttachEngine3D
  Height = 20
  Placement = pos=(31.8198,-31.8198,-18) rot=(0,0,1;3.92699rad)
  Radius = 1.5
FEATURE [Part::Cylinder] Cylinder290  label="Válec290"
  Angle = 360
  AttacherType = Attacher::AttachEngine3D
  Height = 20
  Placement = pos=(31.8198,31.8198,-18) rot=(0,0,-1;0.785398rad)
  Radius = 1.5
FEATURE [Part::Cylinder] Cylinder291  label="Válec291"
  Angle = 360
  AttacherType = Attacher::AttachEngine3D
  Height = 20
  Placement = pos=(1.4e-14,-45,-18) rot=(0,0,1;3.14159rad)
  Radius = 1.5
FEATURE [Part::Cylinder] Cylinder292  label="Válec292"
  Angle = 360
  AttacherType = Attacher::AttachEngine3D
  Height = 3
  Placement = pos=(31.8198,-31.8198,-18) rot=(0,0,1;3.92699rad)
  Radius = 3
FEATURE [Part::Cylinder] Cylinder293  label="Válec293"
  Angle = 360
  AttacherType = Attacher::AttachEngine3D
  Height = 3
  Placement = pos=(-31.8198,-31.8198,-18) rot=(0,0,1;2.35619rad)
  Radius = 3
FEATURE [Part::Cylinder] Cylinder294  label="Válec294"
  Angle = 360
  AttacherType = Attacher::AttachEngine3D
  Height = 3
  Placement = pos=(0,45,-18) rot=(0,0,1;0rad)
  Radius = 3
FEATURE [Part::Cylinder] Cylinder295  label="Válec295"
  Angle = 360
  AttacherType = Attacher::AttachEngine3D
  Height = 3
  Placement = pos=(45,1.9e-14,-18) rot=(0,0,-1;1.5708rad)
  Radius = 3
FEATURE [Part::Cylinder] Cylinder296  label="Válec296"
  Angle = 360
  AttacherType = Attacher::AttachEngine3D
  Height = 3
  Placement = pos=(-45,-6e-15,-18) rot=(0,0,1;1.5708rad)
  Radius = 3
FEATURE [Part::Cylinder] Cylinder297  label="Válec297"
  Angle = 360
  AttacherType = Attacher::AttachEngine3D
  Height = 3
  Placement = pos=(-31.8198,31.8198,-18) rot=(0,0,1;0.785398rad)
  Radius = 3
FEATURE [Part::Cylinder] Cylinder298  label="Válec298"
  Angle = 360
  AttacherType = Attacher::AttachEngine3D
  Height = 3
  Placement = pos=(1.4e-14,-45,-18) rot=(0,0,1;3.14159rad)
  Radius = 3
FEATURE [Part::Cylinder] Cylinder299  label="Válec299"
  Angle = 360
  AttacherType = Attacher::AttachEngine3D
  Height = 3
  Placement = pos=(31.8198,31.8198,-18) rot=(0,0,-1;0.785398rad)
  Radius = 3
FEATURE [Part::Compound] Compound235
  Links = -> [Cylinder281,Cylinder280,Cylinder282,Cylinder283]
  Placement = pos=(0,0,-117) rot=(0,0,1;0rad)
FEATURE [Part::Cut] Cut125
  Base = -> Tube029
  Tool = -> Compound235
FEATURE [Part::Compound] Compound236
  Links = -> [Cylinder286,Cylinder288,Cylinder284,Cylinder285,Cylinder291,Cylinder289,Cylinder287,Cylinder290]
  Placement = pos=(0,0,-87) rot=(0,0,1;0.392699rad)
FEATURE [Part::Cut] Cut127
  Base = -> Cut125
  Tool = -> Compound236
FEATURE [Part::Compound] Compound237
  Links = -> [Cylinder294,Cylinder297,Cylinder296,Cylinder293,Cylinder298,Cylinder292,Cylinder295,Cylinder299]
  Placement = pos=(0,0,-82) rot=(0,0,1;0.392699rad)
FEATURE [Part::Cut] Cut128
  Base = -> Cut127
  Tool = -> Compound237
FEATURE [Part::Chamfer] Chamfer003
  Base = -> Cut128
  Edges = 1 edges r=1: [Edge3]
FEATURE [Part::Chamfer] Chamfer004
  Base = -> Cut126
  Edges = 1 edges r=1: [Edge6]
  Placement = pos=(0,0,-1) rot=(0,0,1;0rad)
FEATURE [Part::Compound] Compound238  label="J-max_undermotor-cover"
  Links = -> [Cut124,Chamfer003,Chamfer004]
  Placement = pos=(0,0,72) rot=(0,0,1;0rad)
FEATURE [Part::Cylinder] Cylinder073  label="Válec073"
  Angle = 360
  AttacherType = Attacher::AttachEngine3D
  Height = 4
  Placement = pos=(1500,0,-4) rot=(0,0,1;0rad)
  Radius = 1.5
FEATURE [Part::Compound] Compound116
  Links = -> [Cylinder073]
  Placement = pos=(2060.63,-1353.48,-2) rot=(0.55557,0.83147,0;3.14159rad)
FEATURE [Part::FeaturePython] Tube036  # WARN: FeaturePython — macro-defined, semantics opaque (R4)
  AttacherType = Attacher::AttachEngine3D
  Height = 15
  InnerRadius = 12
  OuterRadius = 20.1
  Placement = pos=(0,0,17) rot=(0,0,1;0rad)
FEATURE [Part::FeaturePython] Tube037  # WARN: FeaturePython — macro-defined, semantics opaque (R4)
  AttacherType = Attacher::AttachEngine3D
  Height = 9
  InnerRadius = 19.5
  OuterRadius = 24.8
  Placement = pos=(0,0,23) rot=(0,0,1;0rad)
FEATURE [Part::Cylinder] Cylinder600  label="Válec600"
  Angle = 360
  AttacherType = Attacher::AttachEngine3D
  Height = 30
  Placement = pos=(-1.2e-14,-16,2) rot=(0,0,1;1.96349rad)
  Radius = 1.5
FEATURE [Part::Cylinder] Cylinder601  label="Válec601"
  Angle = 360
  AttacherType = Attacher::AttachEngine3D
  Height = 3
  Placement = pos=(-1.2e-14,-16,2) rot=(0,0,1;1.96349rad)
  Radius = 3
FEATURE [Part::Cylinder] Cylinder602  label="Válec602"
  Angle = 360
  AttacherType = Attacher::AttachEngine3D
  Height = 3
  Placement = pos=(2e-15,16,2) rot=(0,0,-1;1.1781rad)
  Radius = 3
FEATURE [Part::Cylinder] Cylinder603  label="Válec603"
  Angle = 360
  AttacherType = Attacher::AttachEngine3D
  Height = 3
  Placement = pos=(-16,7e-15,2) rot=(0,0,1;0.392699rad)
  Radius = 3
FEATURE [Part::Cylinder] Cylinder604  label="Válec604"
  Angle = 360
  AttacherType = Attacher::AttachEngine3D
  Height = 30
  Placement = pos=(16,0,2) rot=(0,0,1;3.53429rad)
  Radius = 1.5
FEATURE [Part::Cylinder] Cylinder605  label="Válec605"
  Angle = 360
  AttacherType = Attacher::AttachEngine3D
  Height = 30
  Placement = pos=(2e-15,16,2) rot=(0,0,-1;1.1781rad)
  Radius = 1.5
FEATURE [Part::Cylinder] Cylinder606  label="Válec606"
  Angle = 360
  AttacherType = Attacher::AttachEngine3D
  Height = 30
  Placement = pos=(-16,7e-15,2) rot=(0,0,1;0.392699rad)
  Radius = 1.5
FEATURE [Part::Compound] Compound647
  Links = -> [Cylinder600,Cylinder606,Cylinder605,Cylinder604]
  Placement = pos=(0,0,-2) rot=(0,0,1;0rad)
FEATURE [Part::Cylinder] Cylinder607  label="Válec607"
  Angle = 360
  AttacherType = Attacher::AttachEngine3D
  Height = 3
  Placement = pos=(16,0,2) rot=(0,0,1;3.53429rad)
  Radius = 3
FEATURE [Part::Compound] Compound646
  Links = -> [Cylinder601,Cylinder603,Cylinder602,Cylinder607]
  Placement = pos=(0,0,27) rot=(0,0,1;0rad)
FEATURE [Part::Cut] Cut276
  Base = -> Tube036
  Tool = -> Compound646
FEATURE [Part::Cut] Cut278
  Base = -> Cut276
  Tool = -> Compound647
FEATURE [Part::Box] Box290  label="Krychle290"
  AttacherType = Attacher::AttachEngine3D
  Height = 2
  Length = 10
  Placement = pos=(-11,3,6) rot=(0,0,1;3.14159rad)
  Width = 6
FEATURE [Part::Cylinder] Cylinder608  label="Válec608"
  Angle = 360
  AttacherType = Attacher::AttachEngine3D
  Height = 30
  Placement = pos=(-1.2e-14,-16,2) rot=(0,0,1;1.96349rad)
  Radius = 1.5
FEATURE [Part::Cylinder] Cylinder609  label="Válec609"
  Angle = 360
  AttacherType = Attacher::AttachEngine3D
  Height = 30
  Placement = pos=(16,0,2) rot=(0,0,1;3.53429rad)
  Radius = 1.5
FEATURE [Part::Cylinder] Cylinder610  label="Válec610"
  Angle = 360
  AttacherType = Attacher::AttachEngine3D
  Height = 30
  Placement = pos=(-16,7e-15,2) rot=(0,0,1;0.392699rad)
  Radius = 1.5
FEATURE [Part::Cylinder] Cylinder611  label="Válec611"
  Angle = 360
  AttacherType = Attacher::AttachEngine3D
  Height = 30
  Placement = pos=(2e-15,16,2) rot=(0,0,-1;1.1781rad)
  Radius = 1.5
FEATURE [Part::Compound] Compound648
  Links = -> [Cylinder608,Cylinder610,Cylinder611,Cylinder609]
  Placement = pos=(0,0,5) rot=(0,0,1;0.785398rad)
FEATURE [Part::Box] Box291  label="Krychle291"
  AttacherType = Attacher::AttachEngine3D
  Height = 2
  Length = 10
  Placement = pos=(11,-3,6) rot=(0,0,1;0rad)
  Width = 6
FEATURE [Part::Box] Box292  label="Krychle292"
  AttacherType = Attacher::AttachEngine3D
  Height = 2
  Length = 10
  Placement = pos=(-3,-11,6) rot=(0,0,-1;1.5708rad)
  Width = 6
FEATURE [Part::Box] Box293  label="Krychle293"
  AttacherType = Attacher::AttachEngine3D
  Height = 2
  Length = 10
  Placement = pos=(3,11,6) rot=(0,0,1;1.5708rad)
  Width = 6
FEATURE [Part::Compound] Compound650
  Links = -> [Box291,Box293,Box290,Box292]
  Placement = pos=(0,0,15) rot=(0,0,1;0.785398rad)
FEATURE [Part::Cut] Cut279
  Base = -> Cut278
  Tool = -> Compound650
FEATURE [Part::Cut] Cut277
  Base = -> Cut279
  Tool = -> Compound648
FEATURE [Part::Compound] Compound649
  Links = -> [Tube037,Cut277]
FEATURE [Part::Chamfer] Chamfer016  label="J-max_arm-bearing-fix"
  Base = -> Compound649
  Edges = 1 edges r=1: [Edge8]
  Placement = pos=(0,0,-24) rot=(1,0,0;3.14159rad)
FEATURE [Part::Box] Box294  label="Krychle294"
  AttacherType = Attacher::AttachEngine3D
  Height = 18
  Length = 32
  Placement = pos=(19,30,5) rot=(0,0,1;0rad)
  Width = 38
FEATURE [Part::Box] Box295  label="Krychle295"
  AttacherType = Attacher::AttachEngine3D
  Height = 20
  Length = 20
  Placement = pos=(-45,28,8) rot=(0,0,1;0rad)
  Width = 200
FEATURE [Part::Cylinder] Cylinder668  label="Válec668"
  Angle = 360
  AttacherType = Attacher::AttachEngine3D
  Height = 20
  Placement = pos=(11,54.5,3) rot=(0,0,1;0rad)
  Radius = 8
FEATURE [Part::Box] Box296  label="Krychle296"
  AttacherType = Attacher::AttachEngine3D
  Height = 18
  Length = 35
  Placement = pos=(10,36,5) rot=(0,0,1;0rad)
  Width = 17
FEATURE [Part::Box] Box297  label="Krychle297"
  AttacherType = Attacher::AttachEngine3D
  Height = 18
  Length = 11
  Placement = pos=(37,0,5) rot=(0,0,1;0rad)
  Width = 38
FEATURE [Part::Box] Box298  label="Krychle298"
  AttacherType = Attacher::AttachEngine3D
  Height = 20
  Length = 20
  Placement = pos=(25,28,8) rot=(0,0,1;0rad)
  Width = 200
FEATURE [Part::Compound] Compound210
  Links = -> [Box298,Box295]
FEATURE [Part::Box] Box299  label="Krychle299"
  AttacherType = Attacher::AttachEngine3D
  Height = 18
  Length = 32
  Placement = pos=(19,30,5) rot=(0,0,1;0rad)
  Width = 38
FEATURE [Part::Cylinder] Cylinder669  label="Válec669"
  Angle = 360
  AttacherType = Attacher::AttachEngine3D
  Height = 20
  Placement = pos=(11,54.5,3) rot=(0,0,1;0rad)
  Radius = 8
FEATURE [Part::Box] Box300  label="Krychle300"
  AttacherType = Attacher::AttachEngine3D
  Height = 18
  Length = 35
  Placement = pos=(10,36,5) rot=(0,0,1;0rad)
  Width = 17
FEATURE [Part::Box] Box301  label="Krychle301"
  AttacherType = Attacher::AttachEngine3D
  Height = 18
  Length = 11
  Placement = pos=(37,0,5) rot=(0,0,1;0rad)
  Width = 36
FEATURE [Part::Cylinder] Cylinder670  label="Válec670"
  Angle = 360
  AttacherType = Attacher::AttachEngine3D
  Height = 150
  Placement = pos=(-57,56,18) rot=(0,1,0;1.5708rad)
  Radius = 2.5
FEATURE [Part::FeaturePython] Tube012  # WARN: FeaturePython — macro-defined, semantics opaque (R4)
  AttacherType = Attacher::AttachEngine3D
  Height = 3
  InnerRadius = 28
  OuterRadius = 48
  Placement = pos=(0,0,5) rot=(0,0,1;0rad)
FEATURE [Part::FeaturePython] Tube013  # WARN: FeaturePython — macro-defined, semantics opaque (R4)
  AttacherType = Attacher::AttachEngine3D
  Height = 15
  InnerRadius = 34
  OuterRadius = 48
  Placement = pos=(0,0,8) rot=(0,0,1;0rad)
FEATURE [Part::Cut] Cut292
  Base = -> Box296
  Tool = -> Cylinder668
FEATURE [Part::MultiFuse] Fusion
  Shapes = -> [Box294,Box297,Cut292]
FEATURE [Part::Mirroring] mirror  label="Fusion (mirrored)"
  Base = (0,0,0)
  Normal = (1,0,0)
  Source = -> Fusion
FEATURE [Part::Cut] Cut293
  Base = -> Box300
  Tool = -> Cylinder669
FEATURE [Part::MultiFuse] Fusion001
  Shapes = -> [Box299,Box301,Cut293]
FEATURE [Part::MultiFuse] Fusion002
  Shapes = -> [Tube013,mirror,Fusion001]
FEATURE [Part::Cut] Cut294
  Base = -> Fusion002
  Tool = -> Compound210
FEATURE [Part::Cylinder] Cylinder671  label="Válec671"
  Angle = 360
  AttacherType = Attacher::AttachEngine3D
  Height = 30
  Placement = pos=(-57,38,18) rot=(0,1,0;1.5708rad)
  Radius = 2.5
FEATURE [Part::Cylinder] Cylinder672  label="Válec672"
  Angle = 360
  AttacherType = Attacher::AttachEngine3D
  Height = 30
  Placement = pos=(28,38,18) rot=(0,1,0;1.5708rad)
  Radius = 2.5
FEATURE [Part::Compound] Compound211
  Links = -> [Cylinder670,Cylinder671,Cylinder672]
FEATURE [Part::Cut] Cut295
  Base = -> Cut294
  Tool = -> Compound211
FEATURE [Part::Cylinder] Cylinder673  label="Válec673"
  Angle = 360
  AttacherType = Attacher::AttachEngine3D
  Height = 30
  Placement = pos=(0,44,10) rot=(0,0,-1;1.1781rad)
  Radius = 1.5
FEATURE [Part::Box] Box302  label="Krychle302"
  AttacherType = Attacher::AttachEngine3D
  Height = 2
  Length = 6
  Placement = pos=(-3,41,16) rot=(0,0,1;0rad)
  Width = 8
FEATURE [Part::Box] Box303  label="Krychle303"
  AttacherType = Attacher::AttachEngine3D
  Height = 2
  Length = 6
  Placement = pos=(-41,-3,16) rot=(0,0,1;1.5708rad)
  Width = 8
FEATURE [Part::Box] Box304  label="Krychle304"
  AttacherType = Attacher::AttachEngine3D
  Height = 2
  Length = 6
  Placement = pos=(3,-41,16) rot=(0,0,1;3.14159rad)
  Width = 8
FEATURE [Part::Box] Box305  label="Krychle305"
  AttacherType = Attacher::AttachEngine3D
  Height = 2
  Length = 6
  Placement = pos=(41,3,16) rot=(0,0,-1;1.5708rad)
  Width = 8
FEATURE [Part::Compound] Compound212
  Links = -> [Box302,Box303,Box304,Box305]
FEATURE [Part::Cut] Cut296
  Base = -> Cut295
  Tool = -> Compound212
FEATURE [Part::Cylinder] Cylinder674  label="Válec674"
  Angle = 360
  AttacherType = Attacher::AttachEngine3D
  Height = 30
  Placement = pos=(-44,0,10) rot=(0,0,1;0.392699rad)
  Radius = 1.5
FEATURE [Part::Cylinder] Cylinder675  label="Válec675"
  Angle = 360
  AttacherType = Attacher::AttachEngine3D
  Height = 30
  Placement = pos=(1.5e-14,-44,10) rot=(0,0,1;1.96349rad)
  Radius = 1.5
FEATURE [Part::Cylinder] Cylinder676  label="Válec676"
  Angle = 360
  AttacherType = Attacher::AttachEngine3D
  Height = 30
  Placement = pos=(44,3.4e-14,10) rot=(0,0,1;3.53429rad)
  Radius = 1.5
FEATURE [Part::Compound] Compound213
  Links = -> [Cylinder673,Cylinder674,Cylinder675,Cylinder676]
FEATURE [Part::Cut] Cut297
  Base = -> Cut296
  Tool = -> Compound213
FEATURE [Part::Box] Box  label="Krychle"
  AttacherType = Attacher::AttachEngine3D
  Height = 2
  Length = 6
  Placement = pos=(-51,58,12) rot=(0,0,1;0rad)
  Width = 6
FEATURE [Part::Cylinder] Cylinder  label="Válec"
  Angle = 360
  AttacherType = Attacher::AttachEngine3D
  Height = 30
  Placement = pos=(-48,61,0) rot=(0,0,1;0rad)
  Radius = 1.5
FEATURE [Part::Box] Box306  label="Krychle306"
  AttacherType = Attacher::AttachEngine3D
  Height = 2
  Length = 6
  Placement = pos=(-25,58,12) rot=(0,0,1;0rad)
  Width = 6
FEATURE [Part::Cylinder] Cylinder677  label="Válec677"
  Angle = 360
  AttacherType = Attacher::AttachEngine3D
  Height = 30
  Placement = pos=(-22,61,0) rot=(0,0,1;0rad)
  Radius = 1.5
FEATURE [Part::Box] Box307  label="Krychle307"
  AttacherType = Attacher::AttachEngine3D
  Height = 2
  Length = 6
  Placement = pos=(45,58,12) rot=(0,0,1;0rad)
  Width = 6
FEATURE [Part::Box] Box308  label="Krychle308"
  AttacherType = Attacher::AttachEngine3D
  Height = 2
  Length = 6
  Placement = pos=(19,58,12) rot=(0,0,1;0rad)
  Width = 6
FEATURE [Part::Box] Box309  label="Krychle309"
  AttacherType = Attacher::AttachEngine3D
  Height = 18
  Length = 3
  Placement = pos=(48,14,5) rot=(0,0,1;0rad)
  Width = 16
FEATURE [Part::Box] Box310  label="Krychle310"
  AttacherType = Attacher::AttachEngine3D
  Height = 18
  Length = 3
  Placement = pos=(-51,14,5) rot=(0,0,1;0rad)
  Width = 16
FEATURE [Part::Cylinder] Cylinder678  label="Válec678"
  Angle = 360
  AttacherType = Attacher::AttachEngine3D
  Height = 30
  Placement = pos=(48,61,0) rot=(0,0,1;0rad)
  Radius = 1.5
FEATURE [Part::Cylinder] Cylinder679  label="Válec679"
  Angle = 360
  AttacherType = Attacher::AttachEngine3D
  Height = 30
  Placement = pos=(22,61,0) rot=(0,0,1;0rad)
  Radius = 1.5
FEATURE [Part::Compound] Compound
  Links = -> [Cylinder,Cylinder677,Cylinder678,Cylinder679]
  Placement = pos=(0,0,7) rot=(0,0,1;0rad)
FEATURE [Part::Compound] Compound664
  Links = -> [Box,Box306,Box307,Box308]
FEATURE [Part::Cut] Cut
  Base = -> Cut297
  Tool = -> Compound664
FEATURE [Part::Cut] Cut298
  Base = -> Cut
  Tool = -> Compound
FEATURE [Part::Chamfer] Chamfer
  Base = -> Box310
  Edges = 1 edges r=2.9: [Edge1]
FEATURE [Part::Chamfer] Chamfer033
  Base = -> Box309
  Edges = 1 edges r=2.9: [Edge5]
FEATURE [Part::Cylinder] Cylinder680  label="Válec680"
  Angle = 360
  AttacherType = Attacher::AttachEngine3D
  Height = 10
  Placement = pos=(-19,56,18) rot=(0,1,0;1.5708rad)
  Radius = 8
FEATURE [Part::Cylinder] Cylinder681  label="Válec681"
  Angle = 360
  AttacherType = Attacher::AttachEngine3D
  Height = 10
  Placement = pos=(9,56,18) rot=(0,1,0;1.5708rad)
  Radius = 8
FEATURE [Part::Compound] Compound665
  Links = -> [Cylinder680,Cylinder681]
FEATURE [Part::Box] Box311  label="Krychle311"
  AttacherType = Attacher::AttachEngine3D
  Height = 2
  Length = 6
  Placement = pos=(-26.8701,-31.1127,16) rot=(0,0,1;2.35619rad)
  Width = 8
FEATURE [Part::Cylinder] Cylinder682  label="Válec682"
  Angle = 360
  AttacherType = Attacher::AttachEngine3D
  Height = 30
  Placement = pos=(-31.1127,-31.1127,10) rot=(0,0,1;1.1781rad)
  Radius = 1.5
FEATURE [Part::Box] Box312  label="Krychle312"
  AttacherType = Attacher::AttachEngine3D
  Height = 2
  Length = 6
  Placement = pos=(31.1127,-26.8701,16) rot=(0,0,1;3.92699rad)
  Width = 8
FEATURE [Part::Compound] Compound652
  Links = -> [Box311,Box312]
FEATURE [Part::Cylinder] Cylinder683  label="Válec683"
  Angle = 360
  AttacherType = Attacher::AttachEngine3D
  Height = 30
  Placement = pos=(31.1127,-31.1127,10) rot=(0,0,1;2.74889rad)
  Radius = 1.5
FEATURE [Part::Compound] Compound667
  Links = -> [Cylinder682,Cylinder683]
FEATURE [Part::Cut] Cut299
  Base = -> Cut298
  Tool = -> Compound665
FEATURE [Part::Chamfer] Chamfer034
  Base = -> Cut299
  Edges = 2 edges r=2: [Edge163,Edge202]
FEATURE [Part::Fillet] Fillet003
  Base = -> Chamfer034
  Edges = 2 edges r=3: [Edge4,Edge291]
FEATURE [Part::Compound] Compound666
  Links = -> [Chamfer,Chamfer033,Fillet003]
FEATURE [Part::Compound] Compound651
  Links = -> [Tube012,Compound666]
FEATURE [Part::Cut] Cut300
  Base = -> Compound651
  Tool = -> Compound652
FEATURE [Part::Cut] Cut301  label="J-max_bear-rotator1"
  Base = -> Cut300
  Tool = -> Compound667
FEATURE [Part::FeaturePython] Tube062  # WARN: FeaturePython — macro-defined, semantics opaque (R4)
  AttacherType = Attacher::AttachEngine3D
  Height = 3
  InnerRadius = 28
  OuterRadius = 48
  Placement = pos=(0,0,5) rot=(0,0,1;0rad)
FEATURE [Part::Compound] Compound668  label="J-max_bear-rotator"
  Links = -> [Tube062,Cut301]
  Placement = pos=(0,0,-24) rot=(0,1,0;3.14159rad)
FEATURE [Part::FeaturePython] Tube035  # WARN: FeaturePython — macro-defined, semantics opaque (R4)
  AttacherType = Attacher::AttachEngine3D
  Height = 8
  InnerRadius = 28
  OuterRadius = 34
  Placement = pos=(0,0,23) rot=(0,0,1;0rad)
FEATURE [Part::Box] Box313  label="Krychle313"
  AttacherType = Attacher::AttachEngine3D
  Height = 20
  Length = 20
  Placement = pos=(-45,28,8) rot=(0,0,1;0rad)
  Width = 200
FEATURE [Part::FeaturePython] Tube063  # WARN: FeaturePython — macro-defined, semantics opaque (R4)
  AttacherType = Attacher::AttachEngine3D
  Height = 8
  InnerRadius = 34
  OuterRadius = 48
  Placement = pos=(0,0,23) rot=(0,0,1;0rad)
FEATURE [Part::Box] Box314  label="Krychle314"
  AttacherType = Attacher::AttachEngine3D
  Height = 8
  Length = 32
  Placement = pos=(19,30,5) rot=(0,0,1;0rad)
  Width = 38
FEATURE [Part::Cylinder] Cylinder612  label="Válec612"
  Angle = 360
  AttacherType = Attacher::AttachEngine3D
  Height = 20
  Placement = pos=(11,54.5,3) rot=(0,0,1;0rad)
  Radius = 8
FEATURE [Part::Box] Box315  label="Krychle315"
  AttacherType = Attacher::AttachEngine3D
  Height = 8
  Length = 35
  Placement = pos=(10,36,5) rot=(0,0,1;0rad)
  Width = 17
FEATURE [Part::Cut] Cut280
  Base = -> Box315
  Tool = -> Cylinder612
FEATURE [Part::Box] Box316  label="Krychle316"
  AttacherType = Attacher::AttachEngine3D
  Height = 8
  Length = 11
  Placement = pos=(37,0,5) rot=(0,0,1;0rad)
  Width = 38
FEATURE [Part::MultiFuse] Fusion015
  Placement = pos=(0,0,18) rot=(0,0,1;0rad)
  Shapes = -> [Box314,Box316,Cut280]
FEATURE [Part::Mirroring] mirror005  label="Fusion (mirrored)005"
  Base = (0,0,0)
  Normal = (1,0,0)
  Source = -> Fusion015
FEATURE [Part::Box] Box317  label="Krychle317"
  AttacherType = Attacher::AttachEngine3D
  Height = 20
  Length = 20
  Placement = pos=(25,28,8) rot=(0,0,1;0rad)
  Width = 200
FEATURE [Part::Compound] Compound655
  Links = -> [Box317,Box313]
FEATURE [Part::Box] Box318  label="Krychle318"
  AttacherType = Attacher::AttachEngine3D
  Height = 8
  Length = 32
  Placement = pos=(19,30,5) rot=(0,0,1;0rad)
  Width = 38
FEATURE [Part::Cylinder] Cylinder613  label="Válec613"
  Angle = 360
  AttacherType = Attacher::AttachEngine3D
  Height = 20
  Placement = pos=(11,54.5,3) rot=(0,0,1;0rad)
  Radius = 8
FEATURE [Part::Box] Box319  label="Krychle319"
  AttacherType = Attacher::AttachEngine3D
  Height = 8
  Length = 35
  Placement = pos=(10,36,5) rot=(0,0,1;0rad)
  Width = 17
FEATURE [Part::Cut] Cut281
  Base = -> Box319
  Tool = -> Cylinder613
FEATURE [Part::Box] Box320  label="Krychle320"
  AttacherType = Attacher::AttachEngine3D
  Height = 8
  Length = 11
  Placement = pos=(37,0,5) rot=(0,0,1;0rad)
  Width = 36
FEATURE [Part::MultiFuse] Fusion016
  Placement = pos=(0,0,18) rot=(0,0,1;0rad)
  Shapes = -> [Box318,Box320,Cut281]
FEATURE [Part::MultiFuse] Fusion017
  Shapes = -> [Tube063,mirror005,Fusion016]
FEATURE [Part::Cut] Cut282
  Base = -> Fusion017
  Tool = -> Compound655
FEATURE [Part::Cylinder] Cylinder614  label="Válec614"
  Angle = 360
  AttacherType = Attacher::AttachEngine3D
  Height = 150
  Placement = pos=(-57,56,18) rot=(0,1,0;1.5708rad)
  Radius = 2.5
FEATURE [Part::Cylinder] Cylinder615  label="Válec615"
  Angle = 360
  AttacherType = Attacher::AttachEngine3D
  Height = 30
  Placement = pos=(-57,38,18) rot=(0,1,0;1.5708rad)
  Radius = 2.5
FEATURE [Part::Cylinder] Cylinder616  label="Válec616"
  Angle = 360
  AttacherType = Attacher::AttachEngine3D
  Height = 30
  Placement = pos=(28,38,18) rot=(0,1,0;1.5708rad)
  Radius = 2.5
FEATURE [Part::Compound] Compound656
  Links = -> [Cylinder614,Cylinder615,Cylinder616]
FEATURE [Part::Cut] Cut283
  Base = -> Cut282
  Tool = -> Compound656
FEATURE [Part::Cylinder] Cylinder617  label="Válec617"
  Angle = 360
  AttacherType = Attacher::AttachEngine3D
  Height = 30
  Placement = pos=(0,44,10) rot=(0,0,-1;1.1781rad)
  Radius = 1.5
FEATURE [Part::Box] Box321  label="Krychle321"
  AttacherType = Attacher::AttachEngine3D
  Height = 2
  Length = 6
  Placement = pos=(-3,41,16) rot=(0,0,1;0rad)
  Width = 8
FEATURE [Part::Box] Box322  label="Krychle322"
  AttacherType = Attacher::AttachEngine3D
  Height = 2
  Length = 6
  Placement = pos=(-41,-3,16) rot=(0,0,1;1.5708rad)
  Width = 8
FEATURE [Part::Box] Box323  label="Krychle323"
  AttacherType = Attacher::AttachEngine3D
  Height = 2
  Length = 6
  Placement = pos=(3,-41,16) rot=(0,0,1;3.14159rad)
  Width = 8
FEATURE [Part::Box] Box324  label="Krychle324"
  AttacherType = Attacher::AttachEngine3D
  Height = 2
  Length = 6
  Placement = pos=(41,3,16) rot=(0,0,-1;1.5708rad)
  Width = 8
FEATURE [Part::Compound] Compound657
  Links = -> [Box321,Box322,Box323,Box324]
FEATURE [Part::Cut] Cut284
  Base = -> Cut283
  Tool = -> Compound657
FEATURE [Part::Cylinder] Cylinder618  label="Válec618"
  Angle = 360
  AttacherType = Attacher::AttachEngine3D
  Height = 30
  Placement = pos=(-44,0,10) rot=(0,0,1;0.392699rad)
  Radius = 1.5
FEATURE [Part::Cylinder] Cylinder619  label="Válec619"
  Angle = 360
  AttacherType = Attacher::AttachEngine3D
  Height = 30
  Placement = pos=(1.5e-14,-44,10) rot=(0,0,1;1.96349rad)
  Radius = 1.5
FEATURE [Part::Cylinder] Cylinder620  label="Válec620"
  Angle = 360
  AttacherType = Attacher::AttachEngine3D
  Height = 30
  Placement = pos=(44,3.4e-14,10) rot=(0,0,1;3.53429rad)
  Radius = 1.5
FEATURE [Part::Compound] Compound658
  Links = -> [Cylinder617,Cylinder618,Cylinder619,Cylinder620]
FEATURE [Part::Cut] Cut302
  Base = -> Cut284
  Tool = -> Compound658
FEATURE [Part::Box] Box325  label="Krychle325"
  AttacherType = Attacher::AttachEngine3D
  Height = 2
  Length = 6
  Placement = pos=(-51,58,12) rot=(0,0,1;0rad)
  Width = 6
FEATURE [Part::Cylinder] Cylinder621  label="Válec621"
  Angle = 360
  AttacherType = Attacher::AttachEngine3D
  Height = 30
  Placement = pos=(-48,61,0) rot=(0,0,1;0rad)
  Radius = 1.5
FEATURE [Part::Box] Box326  label="Krychle326"
  AttacherType = Attacher::AttachEngine3D
  Height = 2
  Length = 6
  Placement = pos=(-25,58,12) rot=(0,0,1;0rad)
  Width = 6
FEATURE [Part::Cylinder] Cylinder622  label="Válec622"
  Angle = 360
  AttacherType = Attacher::AttachEngine3D
  Height = 30
  Placement = pos=(-22,61,0) rot=(0,0,1;0rad)
  Radius = 1.5
FEATURE [Part::Box] Box327  label="Krychle327"
  AttacherType = Attacher::AttachEngine3D
  Height = 2
  Length = 6
  Placement = pos=(45,58,12) rot=(0,0,1;0rad)
  Width = 6
FEATURE [Part::Box] Box328  label="Krychle328"
  AttacherType = Attacher::AttachEngine3D
  Height = 2
  Length = 6
  Placement = pos=(19,58,12) rot=(0,0,1;0rad)
  Width = 6
FEATURE [Part::Compound] Compound669
  Links = -> [Box325,Box326,Box327,Box328]
FEATURE [Part::Cut] Cut286
  Base = -> Cut302
  Tool = -> Compound669
FEATURE [Part::Cylinder] Cylinder684  label="Válec684"
  Angle = 360
  AttacherType = Attacher::AttachEngine3D
  Height = 30
  Placement = pos=(48,61,0) rot=(0,0,1;0rad)
  Radius = 1.5
FEATURE [Part::Cylinder] Cylinder624  label="Válec624"
  Angle = 360
  AttacherType = Attacher::AttachEngine3D
  Height = 30
  Placement = pos=(22,61,0) rot=(0,0,1;0rad)
  Radius = 1.5
FEATURE [Part::Compound] Compound659
  Links = -> [Cylinder621,Cylinder622,Cylinder684,Cylinder624]
  Placement = pos=(0,0,7) rot=(0,0,1;0rad)
FEATURE [Part::Cut] Cut303
  Base = -> Cut286
  Tool = -> Compound659
FEATURE [Part::Cylinder] Cylinder685  label="Válec685"
  Angle = 360
  AttacherType = Attacher::AttachEngine3D
  Height = 10
  Placement = pos=(-19,56,18) rot=(0,1,0;1.5708rad)
  Radius = 8
FEATURE [Part::Cylinder] Cylinder686  label="Válec686"
  Angle = 360
  AttacherType = Attacher::AttachEngine3D
  Height = 10
  Placement = pos=(9,56,18) rot=(0,1,0;1.5708rad)
  Radius = 8
FEATURE [Part::Compound] Compound670
  Links = -> [Cylinder685,Cylinder686]
FEATURE [Part::Cut] Cut288
  Base = -> Cut303
  Tool = -> Compound670
FEATURE [Part::Cylinder] Cylinder687  label="Válec687"
  Angle = 360
  AttacherType = Attacher::AttachEngine3D
  Height = 3
  Placement = pos=(0,44,10) rot=(0,0,-1;1.1781rad)
  Radius = 3
FEATURE [Part::Cylinder] Cylinder634  label="Válec634"
  Angle = 360
  AttacherType = Attacher::AttachEngine3D
  Height = 3
  Placement = pos=(-44,0,10) rot=(0,0,1;0.392699rad)
  Radius = 3
FEATURE [Part::Cylinder] Cylinder635  label="Válec635"
  Angle = 360
  AttacherType = Attacher::AttachEngine3D
  Height = 3
  Placement = pos=(1.5e-14,-44,10) rot=(0,0,1;1.96349rad)
  Radius = 3
FEATURE [Part::Cylinder] Cylinder636  label="Válec636"
  Angle = 360
  AttacherType = Attacher::AttachEngine3D
  Height = 3
  Placement = pos=(44,3.4e-14,10) rot=(0,0,1;3.53429rad)
  Radius = 3
FEATURE [Part::Compound] Compound671
  Links = -> [Cylinder687,Cylinder634,Cylinder635,Cylinder636]
  Placement = pos=(0,0,18) rot=(0,0,1;0rad)
FEATURE [Part::Box] Box329  label="Krychle329"
  AttacherType = Attacher::AttachEngine3D
  Height = 8
  Length = 3
  Placement = pos=(-51,14,23) rot=(0,0,1;0rad)
  Width = 16
FEATURE [Part::Box] Box330  label="Krychle330"
  AttacherType = Attacher::AttachEngine3D
  Height = 8
  Length = 3
  Placement = pos=(48,14,23) rot=(0,0,1;0rad)
  Width = 16
FEATURE [Part::Cylinder] Cylinder637  label="Válec637"
  Angle = 360
  AttacherType = Attacher::AttachEngine3D
  Height = 3
  Placement = pos=(-48,61,0) rot=(0,0,1;0rad)
  Radius = 3
FEATURE [Part::Cylinder] Cylinder688  label="Válec688"
  Angle = 360
  AttacherType = Attacher::AttachEngine3D
  Height = 3
  Placement = pos=(-22,61,0) rot=(0,0,1;0rad)
  Radius = 3
FEATURE [Part::Cylinder] Cylinder689  label="Válec689"
  Angle = 360
  AttacherType = Attacher::AttachEngine3D
  Height = 3
  Placement = pos=(48,61,0) rot=(0,0,1;0rad)
  Radius = 3
FEATURE [Part::Cylinder] Cylinder640  label="Válec640"
  Angle = 360
  AttacherType = Attacher::AttachEngine3D
  Height = 3
  Placement = pos=(22,61,0) rot=(0,0,1;0rad)
  Radius = 3
FEATURE [Part::Cylinder] Cylinder641  label="Válec641"
  Angle = 360
  AttacherType = Attacher::AttachEngine3D
  Height = 30
  Placement = pos=(-31.1127,-31.1127,10) rot=(0,0,1;1.1781rad)
  Radius = 1.5
FEATURE [Part::Cylinder] Cylinder642  label="Válec642"
  Angle = 360
  AttacherType = Attacher::AttachEngine3D
  Height = 30
  Placement = pos=(31.1127,-31.1127,10) rot=(0,0,1;2.74889rad)
  Radius = 1.5
FEATURE [Part::Cylinder] Cylinder643  label="Válec643"
  Angle = 360
  AttacherType = Attacher::AttachEngine3D
  Height = 3
  Placement = pos=(-31.1127,-31.1127,10) rot=(0,0,1;1.1781rad)
  Radius = 3
FEATURE [Part::Cylinder] Cylinder644  label="Válec644"
  Angle = 360
  AttacherType = Attacher::AttachEngine3D
  Height = 3
  Placement = pos=(31.1127,-31.1127,10) rot=(0,0,1;2.74889rad)
  Radius = 3
FEATURE [Part::Compound] Compound672
  Links = -> [Cylinder637,Cylinder688,Cylinder689,Cylinder640]
  Placement = pos=(0,0,28) rot=(0,0,1;0rad)
FEATURE [Part::Compound] Compound673
  Links = -> [Cylinder641,Cylinder642]
FEATURE [Part::Compound] Compound674
  Links = -> [Cylinder643,Cylinder644]
  Placement = pos=(0,0,18) rot=(0,0,1;0rad)
FEATURE [Part::Chamfer] Chamfer035
  Base = -> Box329
  Edges = 1 edges r=2.9: [Edge1]
FEATURE [Part::Chamfer] Chamfer037
  Base = -> Box330
  Edges = 1 edges r=2.9: [Edge5]
FEATURE [Part::Cut] Cut289
  Base = -> Cut288
  Tool = -> Compound671
FEATURE [Part::Cut] Cut304
  Base = -> Cut289
  Tool = -> Compound674
FEATURE [Part::Cut] Cut305
  Base = -> Cut304
  Tool = -> Compound672
FEATURE [Part::Cut] Cut306
  Base = -> Cut305
  Tool = -> Compound673
FEATURE [Part::Chamfer] Chamfer036
  Base = -> Cut306
  Edges = 2 edges r=2: [Edge104,Edge164]
FEATURE [Part::Fillet] Fillet008
  Base = -> Chamfer036
  Edges = 2 edges r=3: [Edge6,Edge219]
FEATURE [Part::Compound] Compound675  label="J-max_bear-cover"
  Links = -> [Tube035,Chamfer035,Chamfer037,Fillet008]
  Placement = pos=(0,0,-24) rot=(0,1,0;3.14159rad)
FEATURE [Part::Box] Box331  label="Krychle331"
  AttacherType = Attacher::AttachEngine3D
  Height = 20
  Length = 20
  Placement = pos=(-45,28,8) rot=(0,0,1;0rad)
  Width = 200
FEATURE [Part::Box] Box332  label="Krychle332"
  AttacherType = Attacher::AttachEngine3D
  Height = 20
  Length = 20
  Placement = pos=(25,28,8) rot=(0,0,1;0rad)
  Width = 200
FEATURE [Part::Compound] Compound676
  Links = -> [Box332,Box331]
  Placement = pos=(0,0,-60) rot=(0,0,1;0rad)
FEATURE [Part::Box] Box333  label="Krychle333"
  AttacherType = Attacher::AttachEngine3D
  Height = 4
  Length = 90
  Placement = pos=(-45,80,-56) rot=(0,0,1;0rad)
  Width = 16
FEATURE [Part::Cylinder] Cylinder774  label="Válec774"
  Angle = 360
  AttacherType = Attacher::AttachEngine3D
  Height = 20
  Placement = pos=(15.75,114,38.52) rot=(0,0.707107,0.707107;3.14159rad)
  Radius = 1.5
FEATURE [Part::Cylinder] Cylinder776  label="Válec776"
  Angle = 360
  AttacherType = Attacher::AttachEngine3D
  Height = 20
  Placement = pos=(15.75,114,59.48) rot=(0,0.707107,0.707107;3.14159rad)
  Radius = 1.5
FEATURE [Part::Compound] Compound536
  Links = -> [Cylinder774,Cylinder776]
  Placement = pos=(-49,0,-96) rot=(0.57735,0.57735,0.57735;2.0944rad)
FEATURE [Part::Box] Box636  label="Krychle636"
  AttacherType = Attacher::AttachEngine3D
  Height = 3
  Length = 16
  Placement = pos=(-33.45,-27.55,31) rot=(0,0,1;0rad)
  Width = 8
FEATURE [Part::Cylinder] Cylinder1598  label="Válec1598"
  Angle = 360
  AttacherType = Attacher::AttachEngine3D
  Height = 4
  Placement = pos=(23.55,23.55,26) rot=(0,0,1;0rad)
  Radius = 5
FEATURE [Part::Cylinder] Cylinder1599  label="Válec1599"
  Angle = 360
  AttacherType = Attacher::AttachEngine3D
  Height = 30
  Placement = pos=(-1.2e-14,-16,2) rot=(0,0,1;1.96349rad)
  Radius = 1.5
FEATURE [Part::Cylinder] Cylinder1600  label="Válec1600"
  Angle = 360
  AttacherType = Attacher::AttachEngine3D
  Height = 20
  Placement = pos=(0,0,15) rot=(0,0,1;0rad)
  Radius = 12
FEATURE [Part::Cylinder] Cylinder1601  label="Válec1601"
  Angle = 360
  AttacherType = Attacher::AttachEngine3D
  Height = 3
  Placement = pos=(2e-15,16,2) rot=(0,0,-1;1.1781rad)
  Radius = 3
FEATURE [Part::Box] Box637  label="Krychle637"
  AttacherType = Attacher::AttachEngine3D
  Height = 3
  Length = 16
  Placement = pos=(17.55,19.55,31) rot=(0,0,1;0rad)
  Width = 8
FEATURE [Part::Cylinder] Cylinder1602  label="Válec1602"
  Angle = 360
  AttacherType = Attacher::AttachEngine3D
  Height = 20
  Placement = pos=(23.55,23.55,20) rot=(0,0,1;0rad)
  Radius = 2.5
FEATURE [Part::Cylinder] Cylinder1603  label="Válec1603"
  Angle = 360
  AttacherType = Attacher::AttachEngine3D
  Height = 30
  Placement = pos=(-16,7e-15,2) rot=(0,0,1;0.392699rad)
  Radius = 1.5
FEATURE [Part::Cylinder] Cylinder1604  label="Válec1604"
  Angle = 360
  AttacherType = Attacher::AttachEngine3D
  Height = 20
  Placement = pos=(-23.55,23.55,20) rot=(0,0,1;0rad)
  Radius = 2.5
FEATURE [Part::Cylinder] Cylinder1605  label="Válec1605"
  Angle = 360
  AttacherType = Attacher::AttachEngine3D
  Height = 4
  Placement = pos=(23.55,-23.55,26) rot=(0,0,1;0rad)
  Radius = 5
FEATURE [Part::Box] Box638  label="Krychle638"
  AttacherType = Attacher::AttachEngine3D
  Height = 8
  Length = 64
  Placement = pos=(-32,-32,26) rot=(0,0,1;0rad)
  Width = 64
FEATURE [Part::Cylinder] Cylinder1606  label="Válec1606"
  Angle = 360
  AttacherType = Attacher::AttachEngine3D
  Height = 3
  Placement = pos=(16,0,2) rot=(0,0,1;3.53429rad)
  Radius = 3
FEATURE [Part::Box] Box639  label="Krychle639"
  AttacherType = Attacher::AttachEngine3D
  Height = 3
  Length = 16
  Placement = pos=(-33.45,19.55,31) rot=(0,0,1;0rad)
  Width = 8
FEATURE [Part::Cylinder] Cylinder1607  label="Válec1607"
  Angle = 360
  AttacherType = Attacher::AttachEngine3D
  Height = 20
  Placement = pos=(23.55,-23.55,20) rot=(0,0,1;0rad)
  Radius = 2.5
FEATURE [Part::Cylinder] Cylinder1608  label="Válec1608"
  Angle = 360
  AttacherType = Attacher::AttachEngine3D
  Height = 20
  Placement = pos=(-23.55,-23.55,20) rot=(0,0,1;0rad)
  Radius = 2.5
FEATURE [Part::Compound] Compound798
  Links = -> [Cylinder1602,Cylinder1604,Cylinder1608,Cylinder1607]
FEATURE [Part::Box] Box640  label="Krychle640"
  AttacherType = Attacher::AttachEngine3D
  Height = 3
  Length = 16
  Placement = pos=(17.55,-27.55,31) rot=(0,0,1;0rad)
  Width = 8
FEATURE [Part::Cylinder] Cylinder1609  label="Válec1609"
  Angle = 360
  AttacherType = Attacher::AttachEngine3D
  Height = 3
  Placement = pos=(-16,7e-15,2) rot=(0,0,1;0.392699rad)
  Radius = 3
FEATURE [Part::Compound] Compound800
  Links = -> [Box637,Box640,Box639,Box636]
FEATURE [Part::Cylinder] Cylinder1610  label="Válec1610"
  Angle = 360
  AttacherType = Attacher::AttachEngine3D
  Height = 4
  Placement = pos=(-23.55,-23.55,26) rot=(0,0,1;0rad)
  Radius = 5
FEATURE [Part::Cylinder] Cylinder1611  label="Válec1611"
  Angle = 360
  AttacherType = Attacher::AttachEngine3D
  Height = 3
  Placement = pos=(-1.2e-14,-16,2) rot=(0,0,1;1.96349rad)
  Radius = 3
FEATURE [Part::Compound] Compound801
  Links = -> [Cylinder1611,Cylinder1609,Cylinder1601,Cylinder1606]
  Placement = pos=(0,0,29) rot=(0,0,1;0.785398rad)
FEATURE [Part::Cylinder] Cylinder1612  label="Válec1612"
  Angle = 360
  AttacherType = Attacher::AttachEngine3D
  Height = 4
  Placement = pos=(-23.55,23.55,26) rot=(0,0,1;0rad)
  Radius = 5
FEATURE [Part::Compound] Compound799
  Links = -> [Cylinder1610,Cylinder1598,Cylinder1605,Cylinder1612]
  Placement = pos=(0,0,-50) rot=(0,0,1;0rad)
FEATURE [Part::Cylinder] Cylinder1613  label="Válec1613"
  Angle = 360
  AttacherType = Attacher::AttachEngine3D
  Height = 30
  Placement = pos=(2e-15,16,2) rot=(0,0,-1;1.1781rad)
  Radius = 1.5
FEATURE [Part::Cylinder] Cylinder1614  label="Válec1614"
  Angle = 360
  AttacherType = Attacher::AttachEngine3D
  Height = 30
  Placement = pos=(16,0,2) rot=(0,0,1;3.53429rad)
  Radius = 1.5
FEATURE [Part::Compound] Compound802
  Links = -> [Cylinder1599,Cylinder1603,Cylinder1613,Cylinder1614]
  Placement = pos=(0,0,14) rot=(0,0,1;0.785398rad)
FEATURE [Part::Cut] Cut173
  Base = -> Box638
  Tool = -> Compound802
FEATURE [Part::Cut] Cut174
  Base = -> Cut173
  Tool = -> Compound801
FEATURE [Part::Cut] Cut177
  Base = -> Cut174
  Tool = -> Compound798
FEATURE [Part::Cut] Cut175
  Base = -> Cut177
  Tool = -> Compound799
FEATURE [Part::Cut] Cut176
  Base = -> Cut175
  Tool = -> Cylinder1600
FEATURE [Part::Cut] Cut178
  Base = -> Cut176
  Tool = -> Compound800
FEATURE [Part::Cut] Cut179
  Base = -> Cut178
  Tool = -> Compound536
FEATURE [Part::Box] Box641  label="Krychle641"
  AttacherType = Attacher::AttachEngine3D
  Height = 9
  Length = 28.8
  Placement = pos=(-14.4,-15.34,34) rot=(0,0,1;0rad)
  Width = 43.38
FEATURE [Part::Cylinder] Cylinder1615  label="Válec1615"
  Angle = 360
  AttacherType = Attacher::AttachEngine3D
  Height = 100
  Radius = 4
FEATURE [Part::Cut] Cut307
  Base = -> Box641
  Placement = pos=(0,90,-86) rot=(0,0,1;0rad)
  Tool = -> Cylinder1615
FEATURE [Part::Box] Box642  label="Krychle642"
  AttacherType = Attacher::AttachEngine3D
  Height = 9
  Length = 28.8
  Placement = pos=(-14.4,-15.34,34) rot=(0,0,1;0rad)
  Width = 34.21
FEATURE [Part::Cylinder] Cylinder1616  label="Válec1616"
  Angle = 360
  AttacherType = Attacher::AttachEngine3D
  Height = 100
  Radius = 4
FEATURE [Part::Cut] Cut308
  Base = -> Box642
  Placement = pos=(0,90,-83) rot=(0,0,1;0rad)
  Tool = -> Cylinder1616
FEATURE [Part::Cylinder] Cylinder1617  label="Válec1617"
  Angle = 360
  AttacherType = Attacher::AttachEngine3D
  Height = 5
  Placement = pos=(0,90,-54) rot=(0,0,1;0rad)
  Radius = 5
FEATURE [Part::Box] Box643  label="Krychle643"
  AttacherType = Attacher::AttachEngine3D
  Height = 4
  Length = 90
  Placement = pos=(-45,80,-56) rot=(0,0,1;0rad)
  Width = 20
FEATURE [Part::Box] Box644  label="Krychle644"
  AttacherType = Attacher::AttachEngine3D
  Height = 4
  Length = 90
  Placement = pos=(-45,80,-32) rot=(0,0,1;0rad)
  Width = 20
FEATURE [Part::Cylinder] Cylinder1618  label="Válec1618"
  Angle = 360
  AttacherType = Attacher::AttachEngine3D
  Height = 6
  Placement = pos=(0,90,-40) rot=(0,0,1;0rad)
  Radius = 8
FEATURE [Part::Cylinder] Cylinder1619  label="Válec1619"
  Angle = 360
  AttacherType = Attacher::AttachEngine3D
  Height = 48
  Placement = pos=(0,90,-55) rot=(0,0,1;0rad)
  Radius = 3
FEATURE [Part::Box] Box645  label="Krychle645"
  AttacherType = Attacher::AttachEngine3D
  Height = 3
  Length = 42
  Placement = pos=(-21,80,-52) rot=(0,0,1;0rad)
  Width = 32
FEATURE [Part::Cylinder] Cylinder1620  label="Válec1620"
  Angle = 360
  AttacherType = Attacher::AttachEngine3D
  Height = 4
  Placement = pos=(0,90,-53) rot=(0,0,1;0rad)
  Radius = 5
FEATURE [Part::Cut] Cut309
  Base = -> Box645
  Tool = -> Cylinder1620
FEATURE [Part::Cut] Cut310
  Base = -> Box643
  Tool = -> Cylinder1617
FEATURE [Part::Box] Box646  label="Krychle646"
  AttacherType = Attacher::AttachEngine3D
  Height = 9
  Length = 28.8
  Placement = pos=(-14.4,-15.34,34) rot=(0,0,1;0rad)
  Width = 34.21
FEATURE [Part::Compound] Compound803
  Links = -> [Box646]
  Placement = pos=(0,90,-83) rot=(0,0,1;0rad)
FEATURE [Part::Box] Box647  label="Krychle647"
  AttacherType = Attacher::AttachEngine3D
  Height = 9
  Length = 42
  Placement = pos=(-21,80,-49) rot=(0,0,1;0rad)
  Width = 20
FEATURE [Part::Cut] Cut311
  Base = -> Box647
  Placement = pos=(0,0,1) rot=(0,0,1;0rad)
  Tool = -> Compound803
FEATURE [Part::Box] Box648  label="Krychle648"
  AttacherType = Attacher::AttachEngine3D
  Height = 2
  Length = 6
  Placement = pos=(-21,82,-56) rot=(0,0,1;0rad)
  Width = 6
FEATURE [Part::Box] Box649  label="Krychle649"
  AttacherType = Attacher::AttachEngine3D
  Height = 2
  Length = 6
  Placement = pos=(-21,92,-56) rot=(0,0,1;0rad)
  Width = 6
FEATURE [Part::Box] Box650  label="Krychle650"
  AttacherType = Attacher::AttachEngine3D
  Height = 2
  Length = 6
  Placement = pos=(15,82,-56) rot=(0,0,1;0rad)
  Width = 6
FEATURE [Part::Box] Box651  label="Krychle651"
  AttacherType = Attacher::AttachEngine3D
  Height = 2
  Length = 6
  Placement = pos=(15,92,-56) rot=(0,0,1;0rad)
  Width = 6
FEATURE [Part::Cylinder] Cylinder1621  label="Válec1621"
  Angle = 360
  AttacherType = Attacher::AttachEngine3D
  Height = 60
  Placement = pos=(18,95,-57) rot=(0,0,1;0rad)
  Radius = 1.5
FEATURE [Part::Cylinder] Cylinder1622  label="Válec1622"
  Angle = 360
  AttacherType = Attacher::AttachEngine3D
  Height = 60
  Placement = pos=(18,85,-57) rot=(0,0,1;0rad)
  Radius = 1.5
FEATURE [Part::Cylinder] Cylinder1623  label="Válec1623"
  Angle = 360
  AttacherType = Attacher::AttachEngine3D
  Height = 60
  Placement = pos=(-18,85,-57) rot=(0,0,1;0rad)
  Radius = 1.5
FEATURE [Part::Cylinder] Cylinder1624  label="Válec1624"
  Angle = 360
  AttacherType = Attacher::AttachEngine3D
  Height = 60
  Placement = pos=(-18,95,-57) rot=(0,0,1;0rad)
  Radius = 1.5
FEATURE [Part::Compound] Compound804
  Links = -> [Cut179]
  Placement = pos=(0,90,-83) rot=(0,0,1;0rad)
FEATURE [Part::Box] Box652  label="Krychle652"
  AttacherType = Attacher::AttachEngine3D
  Height = 6
  Length = 42
  Placement = pos=(-21,80,-38) rot=(0,0,1;0rad)
  Width = 20
FEATURE [Part::Cylinder] Cylinder1625  label="Válec1625"
  Angle = 360
  AttacherType = Attacher::AttachEngine3D
  Height = 48
  Placement = pos=(0,90,-55) rot=(0,0,1;0rad)
  Radius = 3
FEATURE [Part::Cut] Cut312
  Base = -> Box652
  Tool = -> Cylinder1625
FEATURE [Part::Cut] Cut313
  Base = -> Box644
  Tool = -> Cylinder1619
FEATURE [Part::Cylinder] Cylinder1626  label="Válec1626"
  Angle = 360
  AttacherType = Attacher::AttachEngine3D
  Height = 5
  Placement = pos=(0,90,-38) rot=(0,0,1;0rad)
  Radius = 5
FEATURE [Part::Cut] Cut314
  Base = -> Cut312
  Tool = -> Cylinder1626
FEATURE [Part::Box] Box653  label="Krychle653"
  AttacherType = Attacher::AttachEngine3D
  Height = 20
  Length = 28.8
  Placement = pos=(-14.4,-15.34,34) rot=(0,0,1;0rad)
  Width = 34.21
FEATURE [Part::Box] Box654  label="Krychle654"
  AttacherType = Attacher::AttachEngine3D
  Height = 24
  Length = 42
  Placement = pos=(-21,80,-49) rot=(0,0,1;0rad)
  Width = 20
FEATURE [Part::Compound] Compound805
  Links = -> [Box653]
  Placement = pos=(0,90,-83) rot=(0,0,1;0rad)
FEATURE [Part::Cut] Cut315
  Base = -> Box654
  Placement = pos=(0,0,21) rot=(0,0,1;0rad)
  Tool = -> Compound805
FEATURE [Part::Cylinder] Cylinder1627  label="Válec1627"
  Angle = 360
  AttacherType = Attacher::AttachEngine3D
  Height = 48
  Placement = pos=(0,90,-55) rot=(0,0,1;0rad)
  Radius = 2.5
FEATURE [Part::Cut] Cut316
  Base = -> Cut315
  Tool = -> Cylinder1627
FEATURE [Part::Box] Box655  label="Krychle655"
  AttacherType = Attacher::AttachEngine3D
  Height = 1
  Length = 42
  Placement = pos=(-21,80,-39) rot=(0,0,1;0rad)
  Width = 20
FEATURE [Part::Box] Box656  label="Krychle656"
  AttacherType = Attacher::AttachEngine3D
  Height = 1
  Length = 42
  Placement = pos=(-21,80,-49) rot=(0,0,1;0rad)
  Width = 32
FEATURE [Part::Cylinder] Cylinder1628  label="Válec1628"
  Angle = 360
  AttacherType = Attacher::AttachEngine3D
  Height = 48
  Placement = pos=(0,90,-55) rot=(0,0,1;0rad)
  Radius = 7
FEATURE [Part::Cylinder] Cylinder1629  label="Válec1629"
  Angle = 360
  AttacherType = Attacher::AttachEngine3D
  Height = 48
  Placement = pos=(0,90,-55) rot=(0,0,1;0rad)
  Radius = 4
FEATURE [Part::Cut] Cut317
  Base = -> Box655
  Tool = -> Cylinder1628
FEATURE [Part::Cut] Cut318
  Base = -> Box656
  Tool = -> Cylinder1629
FEATURE [Part::Chamfer] Chamfer038
  Base = -> Cut316
  Edges = 2 edges r=6: [Edge6,Edge8]
FEATURE [Part::Compound] Compound806
  Links = -> [Cylinder1621,Cylinder1622,Cylinder1623,Cylinder1624]
FEATURE [Part::Compound] Compound807
  Links = -> [Box648,Box649,Box650,Box651]
  Placement = pos=(0,0,21) rot=(0,0,1;0rad)
FEATURE [Part::Cylinder] Cylinder1630  label="Válec1630"
  Angle = 360
  AttacherType = Attacher::AttachEngine3D
  Height = 60
  Placement = pos=(18,95,-57) rot=(0,0,1;0rad)
  Radius = 1.5
FEATURE [Part::Cylinder] Cylinder1631  label="Válec1631"
  Angle = 360
  AttacherType = Attacher::AttachEngine3D
  Height = 60
  Placement = pos=(18,85,-57) rot=(0,0,1;0rad)
  Radius = 1.5
FEATURE [Part::Cylinder] Cylinder1632  label="Válec1632"
  Angle = 360
  AttacherType = Attacher::AttachEngine3D
  Height = 60
  Placement = pos=(-18,85,-57) rot=(0,0,1;0rad)
  Radius = 1.5
FEATURE [Part::Cylinder] Cylinder1633  label="Válec1633"
  Angle = 360
  AttacherType = Attacher::AttachEngine3D
  Height = 60
  Placement = pos=(-18,95,-57) rot=(0,0,1;0rad)
  Radius = 1.5
FEATURE [Part::Compound] Compound808
  Links = -> [Cylinder1630,Cylinder1631,Cylinder1632,Cylinder1633]
FEATURE [Part::Cut] Cut319
  Base = -> Cut314
  Tool = -> Compound807
FEATURE [Part::Cylinder] Cylinder1634  label="Válec1634"
  Angle = 360
  AttacherType = Attacher::AttachEngine3D
  Height = 60
  Placement = pos=(18,95,-57) rot=(0,0,1;0rad)
  Radius = 1.5
FEATURE [Part::Cylinder] Cylinder1635  label="Válec1635"
  Angle = 360
  AttacherType = Attacher::AttachEngine3D
  Height = 60
  Placement = pos=(18,85,-57) rot=(0,0,1;0rad)
  Radius = 1.5
FEATURE [Part::Cylinder] Cylinder1636  label="Válec1636"
  Angle = 360
  AttacherType = Attacher::AttachEngine3D
  Height = 60
  Placement = pos=(-18,85,-57) rot=(0,0,1;0rad)
  Radius = 1.5
FEATURE [Part::Cylinder] Cylinder1637  label="Válec1637"
  Angle = 360
  AttacherType = Attacher::AttachEngine3D
  Height = 60
  Placement = pos=(-18,95,-57) rot=(0,0,1;0rad)
  Radius = 1.5
FEATURE [Part::Compound] Compound809
  Links = -> [Cylinder1634,Cylinder1635,Cylinder1636,Cylinder1637]
  Placement = pos=(0,0,-16) rot=(0,0,1;0rad)
FEATURE [Part::Cut] Cut320
  Base = -> Cut318
  Tool = -> Compound806
FEATURE [Part::Cut] Cut321
  Base = -> Cut319
  Tool = -> Compound808
FEATURE [Part::Cylinder] Cylinder1638  label="Válec1638"
  Angle = 360
  AttacherType = Attacher::AttachEngine3D
  Height = 60
  Placement = pos=(18,95,-57) rot=(0,0,1;0rad)
  Radius = 1.5
FEATURE [Part::Cylinder] Cylinder1639  label="Válec1639"
  Angle = 360
  AttacherType = Attacher::AttachEngine3D
  Height = 60
  Placement = pos=(18,85,-57) rot=(0,0,1;0rad)
  Radius = 1.5
FEATURE [Part::Cylinder] Cylinder1640  label="Válec1640"
  Angle = 360
  AttacherType = Attacher::AttachEngine3D
  Height = 60
  Placement = pos=(-18,85,-57) rot=(0,0,1;0rad)
  Radius = 1.5
FEATURE [Part::Cylinder] Cylinder1641  label="Válec1641"
  Angle = 360
  AttacherType = Attacher::AttachEngine3D
  Height = 60
  Placement = pos=(-18,95,-57) rot=(0,0,1;0rad)
  Radius = 1.5
FEATURE [Part::Compound] Compound810
  Links = -> [Cylinder1638,Cylinder1639,Cylinder1640,Cylinder1641]
FEATURE [Part::Cut] Cut322  label="J-max_encoder-washer"
  Base = -> Cut317
  Tool = -> Compound810
FEATURE [Part::Cylinder] Cylinder1642  label="Válec1642"
  Angle = 360
  AttacherType = Attacher::AttachEngine3D
  Height = 60
  Placement = pos=(18,95,-57) rot=(0,0,1;0rad)
  Radius = 1.5
FEATURE [Part::Cylinder] Cylinder1643  label="Válec1643"
  Angle = 360
  AttacherType = Attacher::AttachEngine3D
  Height = 60
  Placement = pos=(18,85,-57) rot=(0,0,1;0rad)
  Radius = 1.5
FEATURE [Part::Cylinder] Cylinder1644  label="Válec1644"
  Angle = 360
  AttacherType = Attacher::AttachEngine3D
  Height = 60
  Placement = pos=(-18,85,-57) rot=(0,0,1;0rad)
  Radius = 1.5
FEATURE [Part::Cylinder] Cylinder1645  label="Válec1645"
  Angle = 360
  AttacherType = Attacher::AttachEngine3D
  Height = 60
  Placement = pos=(-18,95,-57) rot=(0,0,1;0rad)
  Radius = 1.5
FEATURE [Part::Compound] Compound811
  Links = -> [Cylinder1642,Cylinder1643,Cylinder1644,Cylinder1645]
FEATURE [Part::Cut] Cut323
  Base = -> Cut311
  Tool = -> Compound811
FEATURE [Part::Cylinder] Cylinder1646  label="Válec1646"
  Angle = 360
  AttacherType = Attacher::AttachEngine3D
  Height = 60
  Placement = pos=(18,95,-57) rot=(0,0,1;0rad)
  Radius = 1.5
FEATURE [Part::Cylinder] Cylinder1647  label="Válec1647"
  Angle = 360
  AttacherType = Attacher::AttachEngine3D
  Height = 60
  Placement = pos=(18,85,-57) rot=(0,0,1;0rad)
  Radius = 1.5
FEATURE [Part::Cylinder] Cylinder1648  label="Válec1648"
  Angle = 360
  AttacherType = Attacher::AttachEngine3D
  Height = 60
  Placement = pos=(-18,85,-57) rot=(0,0,1;0rad)
  Radius = 1.5
FEATURE [Part::Cylinder] Cylinder1649  label="Válec1649"
  Angle = 360
  AttacherType = Attacher::AttachEngine3D
  Height = 60
  Placement = pos=(-18,95,-57) rot=(0,0,1;0rad)
  Radius = 1.5
FEATURE [Part::Compound] Compound812
  Links = -> [Cylinder1646,Cylinder1647,Cylinder1648,Cylinder1649]
FEATURE [Part::Cut] Cut324
  Base = -> Cut313
  Tool = -> Compound812
FEATURE [Part::Cut] Cut325
  Base = -> Chamfer038
  Tool = -> Compound809
FEATURE [Part::Cylinder] Cylinder1650  label="Válec1650"
  Angle = 360
  AttacherType = Attacher::AttachEngine3D
  Height = 60
  Placement = pos=(18,95,-57) rot=(0,0,1;0rad)
  Radius = 1.5
FEATURE [Part::Cylinder] Cylinder1651  label="Válec1651"
  Angle = 360
  AttacherType = Attacher::AttachEngine3D
  Height = 60
  Placement = pos=(18,85,-57) rot=(0,0,1;0rad)
  Radius = 1.5
FEATURE [Part::Cylinder] Cylinder1652  label="Válec1652"
  Angle = 360
  AttacherType = Attacher::AttachEngine3D
  Height = 60
  Placement = pos=(-18,85,-57) rot=(0,0,1;0rad)
  Radius = 1.5
FEATURE [Part::Cylinder] Cylinder1653  label="Válec1653"
  Angle = 360
  AttacherType = Attacher::AttachEngine3D
  Height = 60
  Placement = pos=(-18,95,-57) rot=(0,0,1;0rad)
  Radius = 1.5
FEATURE [Part::Compound] Compound813
  Links = -> [Cylinder1650,Cylinder1651,Cylinder1652,Cylinder1653]
FEATURE [Part::Cut] Cut326
  Base = -> Cut310
  Tool = -> Compound813
FEATURE [Part::Cylinder] Cylinder1654  label="Válec1654"
  Angle = 360
  AttacherType = Attacher::AttachEngine3D
  Height = 60
  Placement = pos=(18,95,-57) rot=(0,0,1;0rad)
  Radius = 1.5
FEATURE [Part::Cylinder] Cylinder1655  label="Válec1655"
  Angle = 360
  AttacherType = Attacher::AttachEngine3D
  Height = 60
  Placement = pos=(18,85,-57) rot=(0,0,1;0rad)
  Radius = 1.5
FEATURE [Part::Cylinder] Cylinder1656  label="Válec1656"
  Angle = 360
  AttacherType = Attacher::AttachEngine3D
  Height = 60
  Placement = pos=(-18,85,-57) rot=(0,0,1;0rad)
  Radius = 1.5
FEATURE [Part::Cylinder] Cylinder1657  label="Válec1657"
  Angle = 360
  AttacherType = Attacher::AttachEngine3D
  Height = 60
  Placement = pos=(-18,95,-57) rot=(0,0,1;0rad)
  Radius = 1.5
FEATURE [Part::Compound] Compound814
  Links = -> [Cylinder1654,Cylinder1655,Cylinder1656,Cylinder1657]
FEATURE [Part::Cut] Cut327
  Base = -> Cut309
  Tool = -> Compound814
FEATURE [Part::Cylinder] Cylinder1658  label="Válec1658"
  Angle = 360
  AttacherType = Attacher::AttachEngine3D
  Height = 3
  Placement = pos=(18,95,-57) rot=(0,0,1;0rad)
  Radius = 3
FEATURE [Part::Cylinder] Cylinder1659  label="Válec1659"
  Angle = 360
  AttacherType = Attacher::AttachEngine3D
  Height = 3
  Placement = pos=(18,85,-57) rot=(0,0,1;0rad)
  Radius = 3
FEATURE [Part::Cylinder] Cylinder1660  label="Válec1660"
  Angle = 360
  AttacherType = Attacher::AttachEngine3D
  Height = 3
  Placement = pos=(-18,85,-57) rot=(0,0,1;0rad)
  Radius = 3
FEATURE [Part::Cylinder] Cylinder1661  label="Válec1661"
  Angle = 360
  AttacherType = Attacher::AttachEngine3D
  Height = 3
  Placement = pos=(-18,95,-57) rot=(0,0,1;0rad)
  Radius = 3
FEATURE [Part::Compound] Compound815
  Links = -> [Cylinder1658,Cylinder1659,Cylinder1660,Cylinder1661]
FEATURE [Part::Cut] Cut328
  Base = -> Cut326
  Tool = -> Compound815
FEATURE [Part::Chamfer] Chamfer039
  Base = -> Cut325
  Edges = 2 edges r=4: [Edge17,Edge20]
FEATURE [Part::Cylinder] Cylinder1662  label="Válec1662"
  Angle = 360
  AttacherType = Attacher::AttachEngine3D
  Height = 5
  Placement = pos=(35,90,-59) rot=(0,0,1;0rad)
  Radius = 5
FEATURE [Part::Cylinder] Cylinder1663  label="Válec1663"
  Angle = 360
  AttacherType = Attacher::AttachEngine3D
  Height = 5
  Placement = pos=(-35,90,-59) rot=(0,0,1;0rad)
  Radius = 5
FEATURE [Part::Cylinder] Cylinder1664  label="Válec1664"
  Angle = 360
  AttacherType = Attacher::AttachEngine3D
  Height = 20
  Placement = pos=(35,90,-59) rot=(0,0,1;0rad)
  Radius = 2.5
FEATURE [Part::Cylinder] Cylinder1665  label="Válec1665"
  Angle = 360
  AttacherType = Attacher::AttachEngine3D
  Height = 20
  Placement = pos=(-35,90,-59) rot=(0,0,1;0rad)
  Radius = 2.5
FEATURE [Part::Compound] Compound816
  Links = -> [Cylinder1662,Cylinder1663]
FEATURE [Part::Compound] Compound817
  Links = -> [Cylinder1664,Cylinder1665]
FEATURE [Part::Cut] Cut329
  Base = -> Cut328
  Tool = -> Compound816
FEATURE [Part::Cut] Cut330
  Base = -> Cut329
  Tool = -> Compound817
FEATURE [Part::Cylinder] Cylinder1666  label="Válec1666"
  Angle = 360
  AttacherType = Attacher::AttachEngine3D
  Height = 5
  Placement = pos=(35,90,-59) rot=(0,0,1;0rad)
  Radius = 5
FEATURE [Part::Cylinder] Cylinder1667  label="Válec1667"
  Angle = 360
  AttacherType = Attacher::AttachEngine3D
  Height = 5
  Placement = pos=(-35,90,-59) rot=(0,0,1;0rad)
  Radius = 5
FEATURE [Part::Compound] Compound818
  Links = -> [Cylinder1666,Cylinder1667]
  Placement = pos=(0,0,29) rot=(0,0,1;0rad)
FEATURE [Part::Cylinder] Cylinder1668  label="Válec1668"
  Angle = 360
  AttacherType = Attacher::AttachEngine3D
  Height = 20
  Placement = pos=(35,90,-59) rot=(0,0,1;0rad)
  Radius = 2.5
FEATURE [Part::Cylinder] Cylinder1669  label="Válec1669"
  Angle = 360
  AttacherType = Attacher::AttachEngine3D
  Height = 20
  Placement = pos=(-35,90,-59) rot=(0,0,1;0rad)
  Radius = 2.5
FEATURE [Part::Compound] Compound819
  Links = -> [Cylinder1668,Cylinder1669]
  Placement = pos=(0,0,18) rot=(0,0,1;0rad)
FEATURE [Part::Cut] Cut331
  Base = -> Cut324
  Tool = -> Compound818
FEATURE [Part::Cut] Cut332
  Base = -> Cut331
  Tool = -> Compound819
FEATURE [Part::Chamfer] Chamfer040
  Base = -> Cut330
  Edges = 2 edges r=4: [Edge3,Edge18]
FEATURE [Part::Chamfer] Chamfer041
  Base = -> Chamfer040
  Edges = 2 edges r=2: [Edge3,Edge21]
FEATURE [Part::Chamfer] Chamfer042
  Base = -> Cut332
  Edges = 2 edges r=4: [Edge3,Edge18]
FEATURE [Part::Chamfer] Chamfer043
  Base = -> Chamfer042
  Edges = 2 edges r=2: [Edge1,Edge6]
FEATURE [Part::Chamfer] Chamfer044
  Base = -> Chamfer039
  Edges = 2 edges r=2: [Edge14,Edge35]
FEATURE [Part::Cylinder] Cylinder1670  label="Válec1670"
  Angle = 360
  AttacherType = Attacher::AttachEngine3D
  Height = 20
  Placement = pos=(15.75,114,39.48) rot=(0,0.707107,0.707107;3.14159rad)
  Radius = 1.5
FEATURE [Part::Cylinder] Cylinder1671  label="Válec1671"
  Angle = 360
  AttacherType = Attacher::AttachEngine3D
  Height = 20
  Placement = pos=(15.75,114,58.525) rot=(0,0.707107,0.707107;3.14159rad)
  Radius = 1.5
FEATURE [Part::Compound] Compound820
  Links = -> [Cylinder1670,Cylinder1671]
  Placement = pos=(-49,0,-96) rot=(0.57735,0.57735,0.57735;2.0944rad)
FEATURE [Part::Compound] Compound821
  Links = -> [Compound820]
  Placement = pos=(0,74,-80) rot=(0,0,1;0rad)
FEATURE [Part::Cylinder] Cylinder1672  label="Válec1672"
  Angle = 360
  AttacherType = Attacher::AttachEngine3D
  Height = 20
  Placement = pos=(15.75,114,58.525) rot=(0,0.707107,0.707107;3.14159rad)
  Radius = 1.5
FEATURE [Part::Cylinder] Cylinder1673  label="Válec1673"
  Angle = 360
  AttacherType = Attacher::AttachEngine3D
  Height = 20
  Placement = pos=(15.75,114,39.475) rot=(0,0.707107,0.707107;3.14159rad)
  Radius = 1.5
FEATURE [Part::Compound] Compound822
  Links = -> [Cylinder1673,Cylinder1672]
  Placement = pos=(-49,0,-96) rot=(0.57735,0.57735,0.57735;2.0944rad)
FEATURE [Part::Compound] Compound823
  Links = -> [Compound822]
  Placement = pos=(0,74,-80) rot=(0,0,1;0rad)
FEATURE [Part::Cut] Cut333
  Base = -> Cut320
  Tool = -> Compound821
FEATURE [Part::Cut] Cut334
  Base = -> Cut327
  Tool = -> Compound823
FEATURE [Part::Compound] Compound825  label="J-max_encoder-inhold2"
  Links = -> [Chamfer043,Chamfer044,Cut321]
FEATURE [Part::Chamfer] Chamfer046
  Base = -> Cut333
  Edges = 2 edges r=4: [Edge3,Edge18]
FEATURE [Part::Cylinder] Cylinder1674  label="Válec1674"
  Angle = 360
  AttacherType = Attacher::AttachEngine3D
  Height = 4
  Placement = pos=(0,90,-53) rot=(0,0,1;0rad)
  Radius = 5
FEATURE [Part::FeaturePython] Tube064  # WARN: FeaturePython — macro-defined, semantics opaque (R4)
  AttacherType = Attacher::AttachEngine3D
  Height = 1
  InnerRadius = 4
  OuterRadius = 5
  Placement = pos=(0,90,-54) rot=(0,0,1;0rad)
FEATURE [Part::Compound] Compound826
  Links = -> [Cut334,Tube064]
FEATURE [Part::Chamfer] Chamfer047
  Base = -> Compound826
  Edges = 2 edges r=4: [Edge3,Edge18]
FEATURE [Part::Chamfer] Chamfer048
  Base = -> Chamfer047
  Edges = 1 edges r=2: [Edge23]
FEATURE [Mesh::Feature] Mesh  label="J-max_encoder-outhold (Meshed)"
FEATURE [Part::FeaturePython] Tube065  # WARN: FeaturePython — macro-defined, semantics opaque (R4)
  AttacherType = Attacher::AttachEngine3D
  Height = 1
  InnerRadius = 4
  OuterRadius = 5
  Placement = pos=(0,90,-34) rot=(0,0,1;0rad)
FEATURE [Part::Compound] Compound828  label="J-max_encoder-inhold"
  Links = -> [Tube065,Compound825]
FEATURE [Part::Compound] Compound829  label="J-max_encoder-sidehold"
  Links = -> [Cut323,Chamfer046]
FEATURE [Part::Cylinder] Cylinder1675  label="Válec1675"
  Angle = 360
  AttacherType = Attacher::AttachEngine3D
  Height = 20
  Placement = pos=(15.75,114,58.525) rot=(0,0.707107,0.707107;3.14159rad)
  Radius = 1.5
FEATURE [Part::Cylinder] Cylinder1676  label="Válec1676"
  Angle = 360
  AttacherType = Attacher::AttachEngine3D
  Height = 20
  Placement = pos=(15.75,114,39.475) rot=(0,0.707107,0.707107;3.14159rad)
  Radius = 1.5
FEATURE [Part::Compound] Compound830
  Links = -> [Cylinder1676,Cylinder1675]
  Placement = pos=(-49,0,-96) rot=(0.57735,0.57735,0.57735;2.0944rad)
FEATURE [Part::Compound] Compound831
  Links = -> [Compound830]
  Placement = pos=(0,74,-72) rot=(0,0,1;0rad)
FEATURE [Part::Cut] Cut335
  Base = -> Chamfer041
  Tool = -> Compound831
FEATURE [Part::Compound] Compound832  label="J-max_encoder-outhold"
  Links = -> [Chamfer048,Cut335]
FEATURE [Mesh::Feature] Mesh001  label="J-max_encoder-washer (Meshed)"
FEATURE [Part::Box] Box208  label="Krychle208"
  AttacherType = Attacher::AttachEngine3D
  Height = 20
  Length = 20
  Placement = pos=(-52,30,40) rot=(0,0,1;0rad)
  Width = 200
FEATURE [Part::Box] Box209  label="Krychle209"
  AttacherType = Attacher::AttachEngine3D
  Height = 20
  Length = 20
  Placement = pos=(32,30,40) rot=(0,0,1;0rad)
  Width = 200
FEATURE [Part::Compound] Compound526
  Links = -> [Box209,Box208]
  Placement = pos=(0,-2,-32) rot=(0,0,1;0rad)
FEATURE [Part::Cylinder] Cylinder1677  label="Válec1677"
  Angle = 360
  AttacherType = Attacher::AttachEngine3D
  Height = 5
  Placement = pos=(0,90,-54) rot=(0,0,1;0rad)
  Radius = 5
FEATURE [Part::Box] Box657  label="Krychle657"
  AttacherType = Attacher::AttachEngine3D
  Height = 4
  Length = 104
  Placement = pos=(-52,80,-56) rot=(0,0,1;0rad)
  Width = 20
FEATURE [Part::Cut] Cut337
  Base = -> Box657
  Tool = -> Cylinder1677
FEATURE [Part::Box] Box658  label="Krychle658"
  AttacherType = Attacher::AttachEngine3D
  Height = 3
  Length = 42
  Placement = pos=(-21,80,-52) rot=(0,0,1;0rad)
  Width = 32
FEATURE [Part::Cylinder] Cylinder1678  label="Válec1678"
  Angle = 360
  AttacherType = Attacher::AttachEngine3D
  Height = 4
  Placement = pos=(0,90,-53) rot=(0,0,1;0rad)
  Radius = 5
FEATURE [Part::Cut] Cut336
  Base = -> Box658
  Tool = -> Cylinder1678
FEATURE [Part::Cylinder] Cylinder1679  label="Válec1679"
  Angle = 360
  AttacherType = Attacher::AttachEngine3D
  Height = 60
  Placement = pos=(18,85,-57) rot=(0,0,1;0rad)
  Radius = 1.5
FEATURE [Part::Cylinder] Cylinder1680  label="Válec1680"
  Angle = 360
  AttacherType = Attacher::AttachEngine3D
  Height = 60
  Placement = pos=(-18,95,-57) rot=(0,0,1;0rad)
  Radius = 1.5
FEATURE [Part::Cylinder] Cylinder1681  label="Válec1681"
  Angle = 360
  AttacherType = Attacher::AttachEngine3D
  Height = 60
  Placement = pos=(18,95,-57) rot=(0,0,1;0rad)
  Radius = 1.5
FEATURE [Part::Cylinder] Cylinder1682  label="Válec1682"
  Angle = 360
  AttacherType = Attacher::AttachEngine3D
  Height = 60
  Placement = pos=(18,85,-57) rot=(0,0,1;0rad)
  Radius = 1.5
FEATURE [Part::Cylinder] Cylinder1683  label="Válec1683"
  Angle = 360
  AttacherType = Attacher::AttachEngine3D
  Height = 60
  Placement = pos=(-18,95,-57) rot=(0,0,1;0rad)
  Radius = 1.5
FEATURE [Part::Cylinder] Cylinder1684  label="Válec1684"
  Angle = 360
  AttacherType = Attacher::AttachEngine3D
  Height = 60
  Placement = pos=(18,95,-57) rot=(0,0,1;0rad)
  Radius = 1.5
FEATURE [Part::Cylinder] Cylinder1685  label="Válec1685"
  Angle = 360
  AttacherType = Attacher::AttachEngine3D
  Height = 60
  Placement = pos=(-18,85,-57) rot=(0,0,1;0rad)
  Radius = 1.5
FEATURE [Part::Compound] Compound833
  Links = -> [Cylinder1681,Cylinder1682,Cylinder1685,Cylinder1683]
FEATURE [Part::Cylinder] Cylinder1686  label="Válec1686"
  Angle = 360
  AttacherType = Attacher::AttachEngine3D
  Height = 60
  Placement = pos=(-18,85,-57) rot=(0,0,1;0rad)
  Radius = 1.5
FEATURE [Part::Compound] Compound835
  Links = -> [Cylinder1684,Cylinder1679,Cylinder1686,Cylinder1680]
FEATURE [Part::Cylinder] Cylinder1687  label="Válec1687"
  Angle = 360
  AttacherType = Attacher::AttachEngine3D
  Height = 5
  Placement = pos=(42,90,-59) rot=(0,0,1;0rad)
  Radius = 5
FEATURE [Part::Cylinder] Cylinder1688  label="Válec1688"
  Angle = 360
  AttacherType = Attacher::AttachEngine3D
  Height = 20
  Placement = pos=(15.75,114,39.475) rot=(0,0.707107,0.707107;3.14159rad)
  Radius = 1.5
FEATURE [Part::Cylinder] Cylinder1689  label="Válec1689"
  Angle = 360
  AttacherType = Attacher::AttachEngine3D
  Height = 20
  Placement = pos=(42,90,-59) rot=(0,0,1;0rad)
  Radius = 2.5
FEATURE [Part::Cylinder] Cylinder1690  label="Válec1690"
  Angle = 360
  AttacherType = Attacher::AttachEngine3D
  Height = 20
  Placement = pos=(-42,90,-59) rot=(0,0,1;0rad)
  Radius = 2.5
FEATURE [Part::Compound] Compound837
  Links = -> [Cylinder1689,Cylinder1690]
FEATURE [Part::Cylinder] Cylinder1691  label="Válec1691"
  Angle = 360
  AttacherType = Attacher::AttachEngine3D
  Height = 20
  Placement = pos=(15.75,114,58.525) rot=(0,0.707107,0.707107;3.14159rad)
  Radius = 1.5
FEATURE [Part::Cylinder] Cylinder1692  label="Válec1692"
  Angle = 360
  AttacherType = Attacher::AttachEngine3D
  Height = 3
  Placement = pos=(-18,85,-57) rot=(0,0,1;0rad)
  Radius = 3
FEATURE [Part::Cylinder] Cylinder1693  label="Válec1693"
  Angle = 360
  AttacherType = Attacher::AttachEngine3D
  Height = 3
  Placement = pos=(-18,95,-57) rot=(0,0,1;0rad)
  Radius = 3
FEATURE [Part::Cylinder] Cylinder1694  label="Válec1694"
  Angle = 360
  AttacherType = Attacher::AttachEngine3D
  Height = 3
  Placement = pos=(18,95,-57) rot=(0,0,1;0rad)
  Radius = 3
FEATURE [Part::Cylinder] Cylinder1695  label="Válec1695"
  Angle = 360
  AttacherType = Attacher::AttachEngine3D
  Height = 3
  Placement = pos=(18,85,-57) rot=(0,0,1;0rad)
  Radius = 3
FEATURE [Part::Compound] Compound834
  Links = -> [Cylinder1694,Cylinder1695,Cylinder1692,Cylinder1693]
FEATURE [Part::Cylinder] Cylinder1696  label="Válec1696"
  Angle = 360
  AttacherType = Attacher::AttachEngine3D
  Height = 5
  Placement = pos=(-42,90,-59) rot=(0,0,1;0rad)
  Radius = 5
FEATURE [Part::Compound] Compound836
  Links = -> [Cylinder1687,Cylinder1696]
FEATURE [Part::Cylinder] Cylinder1697  label="Válec1697"
  Angle = 360
  AttacherType = Attacher::AttachEngine3D
  Height = 20
  Placement = pos=(15.75,114,58.525) rot=(0,0.707107,0.707107;3.14159rad)
  Radius = 1.5
FEATURE [Part::Cylinder] Cylinder1698  label="Válec1698"
  Angle = 360
  AttacherType = Attacher::AttachEngine3D
  Height = 20
  Placement = pos=(15.75,114,39.475) rot=(0,0.707107,0.707107;3.14159rad)
  Radius = 1.5
FEATURE [Part::Cut] Cut339
  Base = -> Cut337
  Tool = -> Compound833
FEATURE [Part::Cut] Cut340
  Base = -> Cut339
  Tool = -> Compound834
FEATURE [Part::Cut] Cut338
  Base = -> Cut340
  Tool = -> Compound836
FEATURE [Part::Cut] Cut341
  Base = -> Cut338
  Tool = -> Compound837
FEATURE [Part::Cut] Cut343
  Base = -> Cut336
  Tool = -> Compound835
FEATURE [Part::Chamfer] Chamfer049
  Base = -> Cut341
  Edges = 2 edges r=4: [Edge3,Edge18]
FEATURE [Part::Chamfer] Chamfer050
  Base = -> Chamfer049
  Edges = 2 edges r=2: [Edge3,Edge21]
FEATURE [Part::Compound] Compound839
  Links = -> [Cylinder1688,Cylinder1691]
  Placement = pos=(-49,0,-96) rot=(0.57735,0.57735,0.57735;2.0944rad)
FEATURE [Part::Compound] Compound842
  Links = -> [Cylinder1698,Cylinder1697]
  Placement = pos=(-49,0,-96) rot=(0.57735,0.57735,0.57735;2.0944rad)
FEATURE [Part::Compound] Compound840
  Links = -> [Compound842]
  Placement = pos=(0,74,-72) rot=(0,0,1;0rad)
FEATURE [Part::Cut] Cut344
  Base = -> Chamfer050
  Tool = -> Compound840
FEATURE [Part::Compound] Compound843
  Links = -> [Compound839]
  Placement = pos=(0,74,-80) rot=(0,0,1;0rad)
FEATURE [Part::Cut] Cut342
  Base = -> Cut343
  Tool = -> Compound843
FEATURE [Part::FeaturePython] Tube066  # WARN: FeaturePython — macro-defined, semantics opaque (R4)
  AttacherType = Attacher::AttachEngine3D
  Height = 1
  InnerRadius = 4
  OuterRadius = 5
  Placement = pos=(0,90,-54) rot=(0,0,1;0rad)
FEATURE [Part::Compound] Compound838
  Links = -> [Cut342,Tube066]
FEATURE [Part::Chamfer] Chamfer052
  Base = -> Compound838
  Edges = 2 edges r=4: [Edge3,Edge18]
FEATURE [Part::Chamfer] Chamfer051
  Base = -> Chamfer052
  Edges = 1 edges r=2: [Edge23]
FEATURE [Part::Compound] Compound841  label="J-midi_encoder-outhold"
  Links = -> [Chamfer051,Cut344]
  Placement = pos=(0,0,60) rot=(0,0,1;0rad)
FEATURE [Mesh::Feature] Mesh002  label="J-midi_encoder-outhold (Meshed)"
FEATURE [Part::Box] Box659  label="Krychle659"
  AttacherType = Attacher::AttachEngine3D
  Height = 4
  Length = 104
  Placement = pos=(-52,80,-32) rot=(0,0,1;0rad)
  Width = 20
FEATURE [Part::Box] Box660  label="Krychle660"
  AttacherType = Attacher::AttachEngine3D
  Height = 6
  Length = 42
  Placement = pos=(-21,80,-38) rot=(0,0,1;0rad)
  Width = 20
FEATURE [Part::Cylinder] Cylinder1699  label="Válec1699"
  Angle = 360
  AttacherType = Attacher::AttachEngine3D
  Height = 48
  Placement = pos=(0,90,-55) rot=(0,0,1;0rad)
  Radius = 3
FEATURE [Part::Cut] Cut347
  Base = -> Box660
  Tool = -> Cylinder1699
FEATURE [Part::Box] Box661  label="Krychle661"
  AttacherType = Attacher::AttachEngine3D
  Height = 2
  Length = 6
  Placement = pos=(-21,82,-56) rot=(0,0,1;0rad)
  Width = 6
FEATURE [Part::Cylinder] Cylinder1700  label="Válec1700"
  Angle = 360
  AttacherType = Attacher::AttachEngine3D
  Height = 5
  Placement = pos=(0,90,-38) rot=(0,0,1;0rad)
  Radius = 5
FEATURE [Part::Cut] Cut346
  Base = -> Cut347
  Tool = -> Cylinder1700
FEATURE [Part::Cylinder] Cylinder1701  label="Válec1701"
  Angle = 360
  AttacherType = Attacher::AttachEngine3D
  Height = 48
  Placement = pos=(0,90,-55) rot=(0,0,1;0rad)
  Radius = 3
FEATURE [Part::Cut] Cut345
  Base = -> Box659
  Tool = -> Cylinder1701
FEATURE [Part::Box] Box662  label="Krychle662"
  AttacherType = Attacher::AttachEngine3D
  Height = 2
  Length = 6
  Placement = pos=(-21,92,-56) rot=(0,0,1;0rad)
  Width = 6
FEATURE [Part::Box] Box663  label="Krychle663"
  AttacherType = Attacher::AttachEngine3D
  Height = 2
  Length = 6
  Placement = pos=(15,92,-56) rot=(0,0,1;0rad)
  Width = 6
FEATURE [Part::Box] Box664  label="Krychle664"
  AttacherType = Attacher::AttachEngine3D
  Height = 2
  Length = 6
  Placement = pos=(15,82,-56) rot=(0,0,1;0rad)
  Width = 6
FEATURE [Part::Compound] Compound848
  Links = -> [Box661,Box662,Box664,Box663]
  Placement = pos=(0,0,21) rot=(0,0,1;0rad)
FEATURE [Part::Box] Box665  label="Krychle665"
  AttacherType = Attacher::AttachEngine3D
  Height = 24
  Length = 42
  Placement = pos=(-21,80,-49) rot=(0,0,1;0rad)
  Width = 20
FEATURE [Part::Cylinder] Cylinder1702  label="Válec1702"
  Angle = 360
  AttacherType = Attacher::AttachEngine3D
  Height = 60
  Placement = pos=(-18,95,-57) rot=(0,0,1;0rad)
  Radius = 1.5
FEATURE [Part::Cylinder] Cylinder1703  label="Válec1703"
  Angle = 360
  AttacherType = Attacher::AttachEngine3D
  Height = 48
  Placement = pos=(0,90,-55) rot=(0,0,1;0rad)
  Radius = 2.5
FEATURE [Part::Cylinder] Cylinder1704  label="Válec1704"
  Angle = 360
  AttacherType = Attacher::AttachEngine3D
  Height = 60
  Placement = pos=(-18,95,-57) rot=(0,0,1;0rad)
  Radius = 1.5
FEATURE [Part::Cylinder] Cylinder1705  label="Válec1705"
  Angle = 360
  AttacherType = Attacher::AttachEngine3D
  Height = 60
  Placement = pos=(18,95,-57) rot=(0,0,1;0rad)
  Radius = 1.5
FEATURE [Part::Cylinder] Cylinder1706  label="Válec1706"
  Angle = 360
  AttacherType = Attacher::AttachEngine3D
  Height = 60
  Placement = pos=(18,95,-57) rot=(0,0,1;0rad)
  Radius = 1.5
FEATURE [Part::Box] Box666  label="Krychle666"
  AttacherType = Attacher::AttachEngine3D
  Height = 20
  Length = 28.8
  Placement = pos=(-14.4,-15.34,34) rot=(0,0,1;0rad)
  Width = 34.21
FEATURE [Part::Compound] Compound846
  Links = -> [Box666]
  Placement = pos=(0,90,-83) rot=(0,0,1;0rad)
FEATURE [Part::Cylinder] Cylinder1707  label="Válec1707"
  Angle = 360
  AttacherType = Attacher::AttachEngine3D
  Height = 60
  Placement = pos=(18,85,-57) rot=(0,0,1;0rad)
  Radius = 1.5
FEATURE [Part::Cylinder] Cylinder1708  label="Válec1708"
  Angle = 360
  AttacherType = Attacher::AttachEngine3D
  Height = 60
  Placement = pos=(-18,85,-57) rot=(0,0,1;0rad)
  Radius = 1.5
FEATURE [Part::Compound] Compound849
  Links = -> [Cylinder1705,Cylinder1707,Cylinder1708,Cylinder1704]
FEATURE [Part::Cylinder] Cylinder1709  label="Válec1709"
  Angle = 360
  AttacherType = Attacher::AttachEngine3D
  Height = 60
  Placement = pos=(18,85,-57) rot=(0,0,1;0rad)
  Radius = 1.5
FEATURE [Part::Cylinder] Cylinder1710  label="Válec1710"
  Angle = 360
  AttacherType = Attacher::AttachEngine3D
  Height = 60
  Placement = pos=(-18,85,-57) rot=(0,0,1;0rad)
  Radius = 1.5
FEATURE [Part::Compound] Compound850
  Links = -> [Cylinder1706,Cylinder1709,Cylinder1710,Cylinder1702]
  Placement = pos=(0,0,-16) rot=(0,0,1;0rad)
FEATURE [Part::Cylinder] Cylinder1711  label="Válec1711"
  Angle = 360
  AttacherType = Attacher::AttachEngine3D
  Height = 60
  Placement = pos=(18,85,-57) rot=(0,0,1;0rad)
  Radius = 1.5
FEATURE [Part::Cylinder] Cylinder1712  label="Válec1712"
  Angle = 360
  AttacherType = Attacher::AttachEngine3D
  Height = 60
  Placement = pos=(-18,85,-57) rot=(0,0,1;0rad)
  Radius = 1.5
FEATURE [Part::Cylinder] Cylinder1713  label="Válec1713"
  Angle = 360
  AttacherType = Attacher::AttachEngine3D
  Height = 60
  Placement = pos=(-18,95,-57) rot=(0,0,1;0rad)
  Radius = 1.5
FEATURE [Part::Cylinder] Cylinder1714  label="Válec1714"
  Angle = 360
  AttacherType = Attacher::AttachEngine3D
  Height = 60
  Placement = pos=(18,95,-57) rot=(0,0,1;0rad)
  Radius = 1.5
FEATURE [Part::Compound] Compound847
  Links = -> [Cylinder1714,Cylinder1711,Cylinder1712,Cylinder1713]
FEATURE [Part::Cylinder] Cylinder1715  label="Válec1715"
  Angle = 360
  AttacherType = Attacher::AttachEngine3D
  Height = 5
  Placement = pos=(-42,90,-59) rot=(0,0,1;0rad)
  Radius = 5
FEATURE [Part::Cylinder] Cylinder1716  label="Válec1716"
  Angle = 360
  AttacherType = Attacher::AttachEngine3D
  Height = 20
  Placement = pos=(-42,90,-59) rot=(0,0,1;0rad)
  Radius = 2.5
FEATURE [Part::Cylinder] Cylinder1717  label="Válec1717"
  Angle = 360
  AttacherType = Attacher::AttachEngine3D
  Height = 20
  Placement = pos=(42,90,-59) rot=(0,0,1;0rad)
  Radius = 2.5
FEATURE [Part::Compound] Compound845
  Links = -> [Cylinder1717,Cylinder1716]
  Placement = pos=(0,0,18) rot=(0,0,1;0rad)
FEATURE [Part::Cylinder] Cylinder1718  label="Válec1718"
  Angle = 360
  AttacherType = Attacher::AttachEngine3D
  Height = 5
  Placement = pos=(42,90,-59) rot=(0,0,1;0rad)
  Radius = 5
FEATURE [Part::Compound] Compound844
  Links = -> [Cylinder1718,Cylinder1715]
  Placement = pos=(0,0,29) rot=(0,0,1;0rad)
FEATURE [Part::Cut] Cut349
  Base = -> Cut346
  Tool = -> Compound848
FEATURE [Part::Cut] Cut351
  Base = -> Cut345
  Tool = -> Compound847
FEATURE [Part::Cut] Cut353
  Base = -> Cut351
  Tool = -> Compound844
FEATURE [Part::Cut] Cut350
  Base = -> Cut353
  Tool = -> Compound845
FEATURE [Part::Cut] Cut354
  Base = -> Box665
  Placement = pos=(0,0,21) rot=(0,0,1;0rad)
  Tool = -> Compound846
FEATURE [Part::Cut] Cut352
  Base = -> Cut354
  Tool = -> Cylinder1703
FEATURE [Part::Chamfer] Chamfer053
  Base = -> Cut352
  Edges = 2 edges r=6: [Edge6,Edge8]
FEATURE [Part::Cut] Cut348
  Base = -> Chamfer053
  Tool = -> Compound850
FEATURE [Part::Chamfer] Chamfer054
  Base = -> Cut348
  Edges = 2 edges r=4: [Edge17,Edge20]
FEATURE [Part::Cut] Cut355
  Base = -> Cut349
  Tool = -> Compound849
FEATURE [Part::Chamfer] Chamfer056
  Base = -> Chamfer054
  Edges = 2 edges r=2: [Edge14,Edge35]
FEATURE [Part::FeaturePython] Tube067  # WARN: FeaturePython — macro-defined, semantics opaque (R4)
  AttacherType = Attacher::AttachEngine3D
  Height = 1
  InnerRadius = 4
  OuterRadius = 5
  Placement = pos=(0,90,-34) rot=(0,0,1;0rad)
FEATURE [Part::Chamfer] Chamfer057
  Base = -> Cut350
  Edges = 2 edges r=4: [Edge3,Edge18]
FEATURE [Part::Chamfer] Chamfer058
  Base = -> Chamfer057
  Edges = 2 edges r=2: [Edge1,Edge6]
FEATURE [Part::Compound] Compound851  label="J-midi_encoder-inhold"
  Links = -> [Cut355,Chamfer056,Tube067,Chamfer058]
  Placement = pos=(0,0,60) rot=(0,0,1;0rad)
FEATURE [Mesh::Feature] Mesh003  label="J-midi_encoder-inhold (Meshed)"
FEATURE [Part::Cylinder] Cylinder1719  label="Válec1719"
  Angle = 360
  AttacherType = Attacher::AttachEngine3D
  Height = 60
  Placement = pos=(-18,85,-57) rot=(0,0,1;0rad)
  Radius = 1.5
FEATURE [Part::Cylinder] Cylinder1720  label="Válec1720"
  Angle = 360
  AttacherType = Attacher::AttachEngine3D
  Height = 48
  Placement = pos=(0,90,-55) rot=(0,0,1;0rad)
  Radius = 7
FEATURE [Part::Cylinder] Cylinder1721  label="Válec1721"
  Angle = 360
  AttacherType = Attacher::AttachEngine3D
  Height = 60
  Placement = pos=(18,85,-57) rot=(0,0,1;0rad)
  Radius = 1.5
FEATURE [Part::Box] Box667  label="Krychle667"
  AttacherType = Attacher::AttachEngine3D
  Height = 1
  Length = 42
  Placement = pos=(-21,80,-39) rot=(0,0,1;0rad)
  Width = 20
FEATURE [Part::Cylinder] Cylinder1722  label="Válec1722"
  Angle = 360
  AttacherType = Attacher::AttachEngine3D
  Height = 60
  Placement = pos=(18,95,-57) rot=(0,0,1;0rad)
  Radius = 1.5
FEATURE [Part::Cylinder] Cylinder1723  label="Válec1723"
  Angle = 360
  AttacherType = Attacher::AttachEngine3D
  Height = 60
  Placement = pos=(-18,95,-57) rot=(0,0,1;0rad)
  Radius = 1.5
FEATURE [Part::Compound] Compound852
  Links = -> [Cylinder1722,Cylinder1721,Cylinder1719,Cylinder1723]
FEATURE [Part::Cut] Cut356
  Base = -> Box667
  Tool = -> Cylinder1720
FEATURE [Part::Cut] Cut357  label="J-midi_encoder-washer"
  Base = -> Cut356
  Placement = pos=(0,0,60) rot=(0,0,1;0rad)
  Tool = -> Compound852
FEATURE [Mesh::Feature] Mesh004  label="J-midi_encoder-washer (Meshed)"
FEATURE [Part::Cylinder] Cylinder1724  label="Válec1724"
  Angle = 360
  AttacherType = Attacher::AttachEngine3D
  Height = 60
  Placement = pos=(-18,95,-57) rot=(0,0,1;0rad)
  Radius = 1.5
FEATURE [Part::Box] Box668  label="Krychle668"
  AttacherType = Attacher::AttachEngine3D
  Height = 9
  Length = 28.8
  Placement = pos=(-14.4,-15.34,34) rot=(0,0,1;0rad)
  Width = 34.21
FEATURE [Part::Compound] Compound853
  Links = -> [Box668]
  Placement = pos=(0,90,-83) rot=(0,0,1;0rad)
FEATURE [Part::Box] Box669  label="Krychle669"
  AttacherType = Attacher::AttachEngine3D
  Height = 9
  Length = 42
  Placement = pos=(-21,80,-49) rot=(0,0,1;0rad)
  Width = 20
FEATURE [Part::Cut] Cut358
  Base = -> Box669
  Placement = pos=(0,0,1) rot=(0,0,1;0rad)
  Tool = -> Compound853
FEATURE [Part::Cylinder] Cylinder1725  label="Válec1725"
  Angle = 360
  AttacherType = Attacher::AttachEngine3D
  Height = 60
  Placement = pos=(18,95,-57) rot=(0,0,1;0rad)
  Radius = 1.5
FEATURE [Part::Cylinder] Cylinder1726  label="Válec1726"
  Angle = 360
  AttacherType = Attacher::AttachEngine3D
  Height = 60
  Placement = pos=(18,85,-57) rot=(0,0,1;0rad)
  Radius = 1.5
FEATURE [Part::Cylinder] Cylinder1727  label="Válec1727"
  Angle = 360
  AttacherType = Attacher::AttachEngine3D
  Height = 60
  Placement = pos=(-18,85,-57) rot=(0,0,1;0rad)
  Radius = 1.5
FEATURE [Part::Compound] Compound854
  Links = -> [Cylinder1725,Cylinder1726,Cylinder1727,Cylinder1724]
FEATURE [Part::Cylinder] Cylinder1728  label="Válec1728"
  Angle = 360
  AttacherType = Attacher::AttachEngine3D
  Height = 48
  Placement = pos=(0,90,-55) rot=(0,0,1;0rad)
  Radius = 4
FEATURE [Part::Box] Box670  label="Krychle670"
  AttacherType = Attacher::AttachEngine3D
  Height = 1
  Length = 42
  Placement = pos=(-21,80,-49) rot=(0,0,1;0rad)
  Width = 32
FEATURE [Part::Cylinder] Cylinder1729  label="Válec1729"
  Angle = 360
  AttacherType = Attacher::AttachEngine3D
  Height = 60
  Placement = pos=(-18,95,-57) rot=(0,0,1;0rad)
  Radius = 1.5
FEATURE [Part::Cylinder] Cylinder1730  label="Válec1730"
  Angle = 360
  AttacherType = Attacher::AttachEngine3D
  Height = 60
  Placement = pos=(18,85,-57) rot=(0,0,1;0rad)
  Radius = 1.5
FEATURE [Part::Cylinder] Cylinder1731  label="Válec1731"
  Angle = 360
  AttacherType = Attacher::AttachEngine3D
  Height = 60
  Placement = pos=(18,95,-57) rot=(0,0,1;0rad)
  Radius = 1.5
FEATURE [Part::Cylinder] Cylinder1732  label="Válec1732"
  Angle = 360
  AttacherType = Attacher::AttachEngine3D
  Height = 60
  Placement = pos=(-18,85,-57) rot=(0,0,1;0rad)
  Radius = 1.5
FEATURE [Part::Compound] Compound855
  Links = -> [Cylinder1731,Cylinder1730,Cylinder1732,Cylinder1729]
FEATURE [Part::Cylinder] Cylinder1733  label="Válec1733"
  Angle = 360
  AttacherType = Attacher::AttachEngine3D
  Height = 20
  Placement = pos=(15.75,114,39.48) rot=(0,0.707107,0.707107;3.14159rad)
  Radius = 1.5
FEATURE [Part::Cylinder] Cylinder1734  label="Válec1734"
  Angle = 360
  AttacherType = Attacher::AttachEngine3D
  Height = 20
  Placement = pos=(15.75,114,58.525) rot=(0,0.707107,0.707107;3.14159rad)
  Radius = 1.5
FEATURE [Part::Cut] Cut361
  Base = -> Box670
  Tool = -> Cylinder1728
FEATURE [Part::Cut] Cut359
  Base = -> Cut361
  Tool = -> Compound854
FEATURE [Part::Cut] Cut362
  Base = -> Cut358
  Tool = -> Compound855
FEATURE [Part::Compound] Compound856
  Links = -> [Cylinder1733,Cylinder1734]
  Placement = pos=(-49,0,-96) rot=(0.57735,0.57735,0.57735;2.0944rad)
FEATURE [Part::Compound] Compound857
  Links = -> [Compound856]
  Placement = pos=(0,74,-80) rot=(0,0,1;0rad)
FEATURE [Part::Cut] Cut360
  Base = -> Cut359
  Tool = -> Compound857
FEATURE [Part::Chamfer] Chamfer059
  Base = -> Cut360
  Edges = 2 edges r=4: [Edge3,Edge18]
FEATURE [Part::Compound] Compound858  label="J-midi_encoder-sidehold"
  Links = -> [Cut362,Chamfer059]
  Placement = pos=(0,0,60) rot=(0,0,1;0rad)
FEATURE [Mesh::Feature] Mesh005  label="J-midi_encoder-sidehold (Meshed)"
